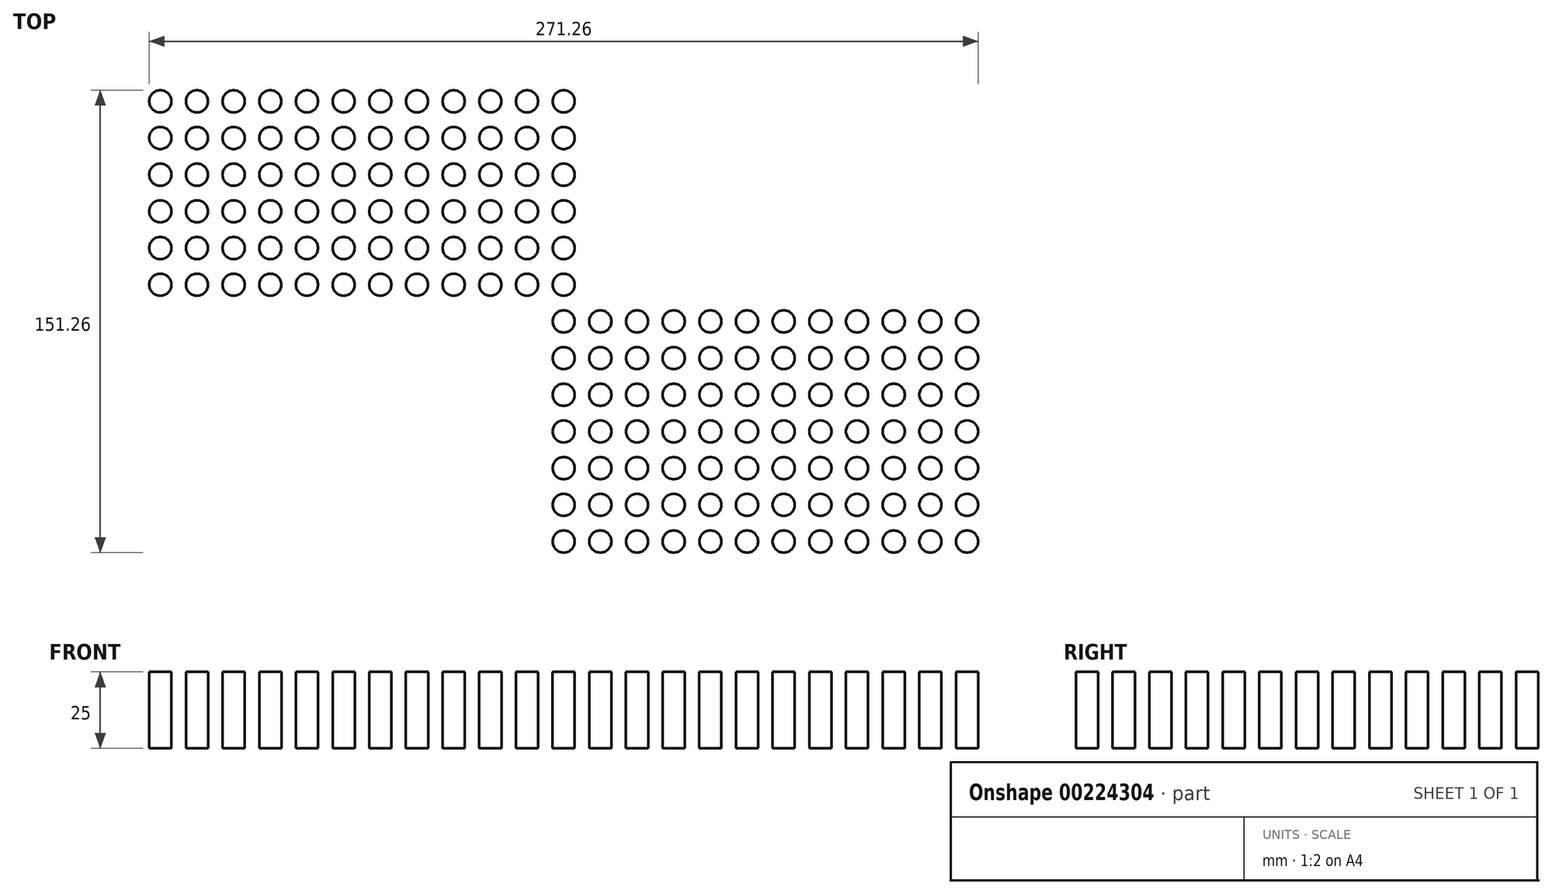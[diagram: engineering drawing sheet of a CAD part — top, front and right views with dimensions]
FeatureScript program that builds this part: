
annotation { "Feature Type Name" : "Feature", "Feature Type Description" : "" }
export const myFeature = defineFeature(function(context is Context, id is Id, definition is map)
    precondition{}
    {
        {
            var Q0;
            Q0=qCreatedBy(makeId("Top.planeOp"),FACE);
            var sketch = newSketch(context, id + "F0", { "sketchPlane" : qUnion([Q0])});
            skLineSegment(sketch, "E0.bottom", {"start": v(140, 90) * mm, "end": v(-140, 90) * mm});
            skLineSegment(sketch, "E0.top", {"start": v(140, -90) * mm, "end": v(-140, -90) * mm});
            skLineSegment(sketch, "E0.left", {"start": v(150, 80) * mm, "end": v(150, -80) * mm});
            skLineSegment(sketch, "E0.right", {"start": v(-150, 80) * mm, "end": v(-150, -80) * mm});
            skPoint(sketch, "E0.middle", {"position": v(0, 0) * mm});
            skPoint(sketch, "E1.visualSharp", {"position": v(-150, 90) * mm});
            skArc(sketch, "E1.filletArc", {"start": v(-140, 90) * mm, "mid": v(-147.07, 87.07) * mm, "end": v(-150, 80) * mm});
            skPoint(sketch, "E2.visualSharp", {"position": v(150, 90) * mm});
            skArc(sketch, "E2.filletArc", {"start": v(150, 80) * mm, "mid": v(147.07, 87.07) * mm, "end": v(140, 90) * mm});
            skPoint(sketch, "E3.visualSharp", {"position": v(150, -90) * mm});
            skArc(sketch, "E3.filletArc", {"start": v(140, -90) * mm, "mid": v(147.07, -87.07) * mm, "end": v(150, -80) * mm});
            skPoint(sketch, "E4.visualSharp", {"position": v(-150, -90) * mm});
            skArc(sketch, "E4.filletArc", {"start": v(-150, -80) * mm, "mid": v(-147.07, -87.07) * mm, "end": v(-140, -90) * mm});
            skSolve(sketch);
        }
        {
            var Q0;
            Q0=makeQuery(id+"F0.imprint","IMPRINT",FACE,{"disambiguationData":[TD([[makeQuery(id+"F0.imprint","IMPRINT",EDGE,{"derivedFrom":sQuery(id+"F0.wireOp",EDGE,"E0.bottom")}),1.0]])]});
            extrude(context, id + "F1", {"entities" : qUnion([Q0]), "depth" : 25 * mm});
        }
        {
            var Q0;
            Q0=makeQuery(id+"F1.opExtrude","CAP_FACE",FACE,{"disambiguationData":[OSD([sQuery(id+"F0.wireOp",EDGE,"E0.bottom"),sQuery(id+"F0.wireOp",EDGE,"E0.top"),sQuery(id+"F0.wireOp",EDGE,"E0.left"),sQuery(id+"F0.wireOp",EDGE,"E0.right"),sQuery(id+"F0.wireOp",EDGE,"E1.filletArc"),sQuery(id+"F0.wireOp",EDGE,"E2.filletArc"),sQuery(id+"F0.wireOp",EDGE,"E3.filletArc"),sQuery(id+"F0.wireOp",EDGE,"E4.filletArc")])],"isStart":false});
            var sketch = newSketch(context, id + "F2", { "sketchPlane" : qUnion([Q0])});
            skCircle(sketch, "E5", {"center": v(0, 0) * mm, "radius": 3.63 * mm});
            skCircle(sketch, "E6.0.1.0", {"center": v(0, 12) * mm, "radius": 3.63 * mm});
            skCircle(sketch, "E6.0.2.0", {"center": v(0, 24) * mm, "radius": 3.63 * mm});
            skCircle(sketch, "E6.0.3.0", {"center": v(0, 36) * mm, "radius": 3.63 * mm});
            skCircle(sketch, "E6.0.4.0", {"center": v(0, 48) * mm, "radius": 3.63 * mm});
            skCircle(sketch, "E6.0.5.0", {"center": v(0, 60) * mm, "radius": 3.63 * mm});
            skCircle(sketch, "E6.0.6.0", {"center": v(0, 72) * mm, "radius": 3.63 * mm});
            skCircle(sketch, "E6.1.0.0", {"center": v(12, 0) * mm, "radius": 3.63 * mm});
            skCircle(sketch, "E6.1.1.0", {"center": v(12, 12) * mm, "radius": 3.63 * mm});
            skCircle(sketch, "E6.1.2.0", {"center": v(12, 24) * mm, "radius": 3.63 * mm});
            skCircle(sketch, "E6.1.3.0", {"center": v(12, 36) * mm, "radius": 3.63 * mm});
            skCircle(sketch, "E6.1.4.0", {"center": v(12, 48) * mm, "radius": 3.63 * mm});
            skCircle(sketch, "E6.1.5.0", {"center": v(12, 60) * mm, "radius": 3.63 * mm});
            skCircle(sketch, "E6.1.6.0", {"center": v(12, 72) * mm, "radius": 3.63 * mm});
            skCircle(sketch, "E6.2.0.0", {"center": v(24, 0) * mm, "radius": 3.63 * mm});
            skCircle(sketch, "E6.2.1.0", {"center": v(24, 12) * mm, "radius": 3.63 * mm});
            skCircle(sketch, "E6.2.2.0", {"center": v(24, 24) * mm, "radius": 3.63 * mm});
            skCircle(sketch, "E6.2.3.0", {"center": v(24, 36) * mm, "radius": 3.63 * mm});
            skCircle(sketch, "E6.2.4.0", {"center": v(24, 48) * mm, "radius": 3.63 * mm});
            skCircle(sketch, "E6.2.5.0", {"center": v(24, 60) * mm, "radius": 3.63 * mm});
            skCircle(sketch, "E6.2.6.0", {"center": v(24, 72) * mm, "radius": 3.63 * mm});
            skCircle(sketch, "E6.3.0.0", {"center": v(36, 0) * mm, "radius": 3.63 * mm});
            skCircle(sketch, "E6.3.1.0", {"center": v(36, 12) * mm, "radius": 3.63 * mm});
            skCircle(sketch, "E6.3.2.0", {"center": v(36, 24) * mm, "radius": 3.63 * mm});
            skCircle(sketch, "E6.3.3.0", {"center": v(36, 36) * mm, "radius": 3.63 * mm});
            skCircle(sketch, "E6.3.4.0", {"center": v(36, 48) * mm, "radius": 3.63 * mm});
            skCircle(sketch, "E6.3.5.0", {"center": v(36, 60) * mm, "radius": 3.63 * mm});
            skCircle(sketch, "E6.3.6.0", {"center": v(36, 72) * mm, "radius": 3.63 * mm});
            skCircle(sketch, "E6.4.0.0", {"center": v(48, 0) * mm, "radius": 3.63 * mm});
            skCircle(sketch, "E6.4.1.0", {"center": v(48, 12) * mm, "radius": 3.63 * mm});
            skCircle(sketch, "E6.4.2.0", {"center": v(48, 24) * mm, "radius": 3.63 * mm});
            skCircle(sketch, "E6.4.3.0", {"center": v(48, 36) * mm, "radius": 3.63 * mm});
            skCircle(sketch, "E6.4.4.0", {"center": v(48, 48) * mm, "radius": 3.63 * mm});
            skCircle(sketch, "E6.4.5.0", {"center": v(48, 60) * mm, "radius": 3.63 * mm});
            skCircle(sketch, "E6.4.6.0", {"center": v(48, 72) * mm, "radius": 3.63 * mm});
            skCircle(sketch, "E6.5.0.0", {"center": v(60, 0) * mm, "radius": 3.63 * mm});
            skCircle(sketch, "E6.5.1.0", {"center": v(60, 12) * mm, "radius": 3.63 * mm});
            skCircle(sketch, "E6.5.2.0", {"center": v(60, 24) * mm, "radius": 3.63 * mm});
            skCircle(sketch, "E6.5.3.0", {"center": v(60, 36) * mm, "radius": 3.63 * mm});
            skCircle(sketch, "E6.5.4.0", {"center": v(60, 48) * mm, "radius": 3.63 * mm});
            skCircle(sketch, "E6.5.5.0", {"center": v(60, 60) * mm, "radius": 3.63 * mm});
            skCircle(sketch, "E6.5.6.0", {"center": v(60, 72) * mm, "radius": 3.63 * mm});
            skCircle(sketch, "E6.6.0.0", {"center": v(72, 0) * mm, "radius": 3.63 * mm});
            skCircle(sketch, "E6.6.1.0", {"center": v(72, 12) * mm, "radius": 3.63 * mm});
            skCircle(sketch, "E6.6.2.0", {"center": v(72, 24) * mm, "radius": 3.63 * mm});
            skCircle(sketch, "E6.6.3.0", {"center": v(72, 36) * mm, "radius": 3.63 * mm});
            skCircle(sketch, "E6.6.4.0", {"center": v(72, 48) * mm, "radius": 3.63 * mm});
            skCircle(sketch, "E6.6.5.0", {"center": v(72, 60) * mm, "radius": 3.63 * mm});
            skCircle(sketch, "E6.6.6.0", {"center": v(72, 72) * mm, "radius": 3.63 * mm});
            skCircle(sketch, "E6.7.0.0", {"center": v(84, 0) * mm, "radius": 3.63 * mm});
            skCircle(sketch, "E6.7.1.0", {"center": v(84, 12) * mm, "radius": 3.63 * mm});
            skCircle(sketch, "E6.7.2.0", {"center": v(84, 24) * mm, "radius": 3.63 * mm});
            skCircle(sketch, "E6.7.3.0", {"center": v(84, 36) * mm, "radius": 3.63 * mm});
            skCircle(sketch, "E6.7.4.0", {"center": v(84, 48) * mm, "radius": 3.63 * mm});
            skCircle(sketch, "E6.7.5.0", {"center": v(84, 60) * mm, "radius": 3.63 * mm});
            skCircle(sketch, "E6.7.6.0", {"center": v(84, 72) * mm, "radius": 3.63 * mm});
            skCircle(sketch, "E6.8.0.0", {"center": v(96, 0) * mm, "radius": 3.63 * mm});
            skCircle(sketch, "E6.8.1.0", {"center": v(96, 12) * mm, "radius": 3.63 * mm});
            skCircle(sketch, "E6.8.2.0", {"center": v(96, 24) * mm, "radius": 3.63 * mm});
            skCircle(sketch, "E6.8.3.0", {"center": v(96, 36) * mm, "radius": 3.63 * mm});
            skCircle(sketch, "E6.8.4.0", {"center": v(96, 48) * mm, "radius": 3.63 * mm});
            skCircle(sketch, "E6.8.5.0", {"center": v(96, 60) * mm, "radius": 3.63 * mm});
            skCircle(sketch, "E6.8.6.0", {"center": v(96, 72) * mm, "radius": 3.63 * mm});
            skCircle(sketch, "E6.9.0.0", {"center": v(108, 0) * mm, "radius": 3.63 * mm});
            skCircle(sketch, "E6.9.1.0", {"center": v(108, 12) * mm, "radius": 3.63 * mm});
            skCircle(sketch, "E6.9.2.0", {"center": v(108, 24) * mm, "radius": 3.63 * mm});
            skCircle(sketch, "E6.9.3.0", {"center": v(108, 36) * mm, "radius": 3.63 * mm});
            skCircle(sketch, "E6.9.4.0", {"center": v(108, 48) * mm, "radius": 3.63 * mm});
            skCircle(sketch, "E6.9.5.0", {"center": v(108, 60) * mm, "radius": 3.63 * mm});
            skCircle(sketch, "E6.9.6.0", {"center": v(108, 72) * mm, "radius": 3.63 * mm});
            skCircle(sketch, "E6.10.0.0", {"center": v(120, 0) * mm, "radius": 3.63 * mm});
            skCircle(sketch, "E6.10.1.0", {"center": v(120, 12) * mm, "radius": 3.63 * mm});
            skCircle(sketch, "E6.10.2.0", {"center": v(120, 24) * mm, "radius": 3.63 * mm});
            skCircle(sketch, "E6.10.3.0", {"center": v(120, 36) * mm, "radius": 3.63 * mm});
            skCircle(sketch, "E6.10.4.0", {"center": v(120, 48) * mm, "radius": 3.63 * mm});
            skCircle(sketch, "E6.10.5.0", {"center": v(120, 60) * mm, "radius": 3.63 * mm});
            skCircle(sketch, "E6.10.6.0", {"center": v(120, 72) * mm, "radius": 3.63 * mm});
            skCircle(sketch, "E6.11.0.0", {"center": v(132, 0) * mm, "radius": 3.63 * mm});
            skCircle(sketch, "E6.11.1.0", {"center": v(132, 12) * mm, "radius": 3.63 * mm});
            skCircle(sketch, "E6.11.2.0", {"center": v(132, 24) * mm, "radius": 3.63 * mm});
            skCircle(sketch, "E6.11.3.0", {"center": v(132, 36) * mm, "radius": 3.63 * mm});
            skCircle(sketch, "E6.11.4.0", {"center": v(132, 48) * mm, "radius": 3.63 * mm});
            skCircle(sketch, "E6.11.5.0", {"center": v(132, 60) * mm, "radius": 3.63 * mm});
            skCircle(sketch, "E6.11.6.0", {"center": v(132, 72) * mm, "radius": 3.63 * mm});
            skLineSegment(sketch, "E6.direction1", {"start": v(0, 0) * mm, "end": v(12, 0) * mm, "construction": true});
            skLineSegment(sketch, "E6.direction2", {"start": v(0, 0) * mm, "end": v(0, 12) * mm, "construction": true});
            skCircle(sketch, "E7.MirrorC", {"center": v(-84, 24) * mm, "radius": 3.63 * mm});
            skCircle(sketch, "E8.MirrorC", {"center": v(-108, 48) * mm, "radius": 3.63 * mm});
            skCircle(sketch, "E9.MirrorC", {"center": v(-132, 72) * mm, "radius": 3.63 * mm});
            skCircle(sketch, "E10.MirrorC", {"center": v(-24, 60) * mm, "radius": 3.63 * mm});
            skCircle(sketch, "E11.MirrorC", {"center": v(-60, 0) * mm, "radius": 3.63 * mm});
            skCircle(sketch, "E12.MirrorC", {"center": v(-36, 60) * mm, "radius": 3.63 * mm});
            skCircle(sketch, "E13.MirrorC", {"center": v(-72, 0) * mm, "radius": 3.63 * mm});
            skCircle(sketch, "E14.MirrorC", {"center": v(-96, 24) * mm, "radius": 3.63 * mm});
            skCircle(sketch, "E15.MirrorC", {"center": v(-120, 48) * mm, "radius": 3.63 * mm});
            skCircle(sketch, "E16.MirrorC", {"center": v(-84, 12) * mm, "radius": 3.63 * mm});
            skCircle(sketch, "E17.MirrorC", {"center": v(-108, 36) * mm, "radius": 3.63 * mm});
            skCircle(sketch, "E18.MirrorC", {"center": v(-132, 60) * mm, "radius": 3.63 * mm});
            skCircle(sketch, "E19.MirrorC", {"center": v(-24, 48) * mm, "radius": 3.63 * mm});
            skCircle(sketch, "E20.MirrorC", {"center": v(-48, 72) * mm, "radius": 3.63 * mm});
            skCircle(sketch, "E21.MirrorC", {"center": v(-12, 60) * mm, "radius": 3.63 * mm});
            skCircle(sketch, "E22.MirrorC", {"center": v(-36, 48) * mm, "radius": 3.63 * mm});
            skCircle(sketch, "E23.MirrorC", {"center": v(-60, 72) * mm, "radius": 3.63 * mm});
            skCircle(sketch, "E24.MirrorC", {"center": v(-96, 12) * mm, "radius": 3.63 * mm});
            skCircle(sketch, "E25.MirrorC", {"center": v(-120, 36) * mm, "radius": 3.63 * mm});
            skCircle(sketch, "E26.MirrorC", {"center": v(-12, 48) * mm, "radius": 3.63 * mm});
            skCircle(sketch, "E27.MirrorC", {"center": v(-12, 36) * mm, "radius": 3.63 * mm});
            skCircle(sketch, "E28.MirrorC", {"center": v(-12, 24) * mm, "radius": 3.63 * mm});
            skCircle(sketch, "E29.MirrorC", {"center": v(-12, 12) * mm, "radius": 3.63 * mm});
            skCircle(sketch, "E30.MirrorC", {"center": v(-12, 0) * mm, "radius": 3.63 * mm});
            skCircle(sketch, "E31.MirrorC", {"center": v(-24, 12) * mm, "radius": 3.63 * mm});
            skCircle(sketch, "E32.MirrorC", {"center": v(-24, 0) * mm, "radius": 3.63 * mm});
            skCircle(sketch, "E33.MirrorC", {"center": v(-12, 72) * mm, "radius": 3.63 * mm});
            skCircle(sketch, "E34.MirrorC", {"center": v(-84, 0) * mm, "radius": 3.63 * mm});
            skCircle(sketch, "E35.MirrorC", {"center": v(-108, 24) * mm, "radius": 3.63 * mm});
            skCircle(sketch, "E36.MirrorC", {"center": v(-132, 48) * mm, "radius": 3.63 * mm});
            skCircle(sketch, "E37.MirrorC", {"center": v(-24, 36) * mm, "radius": 3.63 * mm});
            skCircle(sketch, "E38.MirrorC", {"center": v(-48, 60) * mm, "radius": 3.63 * mm});
            skCircle(sketch, "E39.MirrorC", {"center": v(-36, 36) * mm, "radius": 3.63 * mm});
            skCircle(sketch, "E40.MirrorC", {"center": v(-60, 60) * mm, "radius": 3.63 * mm});
            skCircle(sketch, "E41.MirrorC", {"center": v(-96, 0) * mm, "radius": 3.63 * mm});
            skCircle(sketch, "E42.MirrorC", {"center": v(-120, 24) * mm, "radius": 3.63 * mm});
            skCircle(sketch, "E43.MirrorC", {"center": v(-24, 24) * mm, "radius": 3.63 * mm});
            skCircle(sketch, "E44.MirrorC", {"center": v(-48, 48) * mm, "radius": 3.63 * mm});
            skCircle(sketch, "E45.MirrorC", {"center": v(-36, 24) * mm, "radius": 3.63 * mm});
            skCircle(sketch, "E46.MirrorC", {"center": v(-60, 48) * mm, "radius": 3.63 * mm});
            skCircle(sketch, "E47.MirrorC", {"center": v(-84, 72) * mm, "radius": 3.63 * mm});
            skCircle(sketch, "E48.MirrorC", {"center": v(-120, 12) * mm, "radius": 3.63 * mm});
            skCircle(sketch, "E49.MirrorC", {"center": v(-72, 72) * mm, "radius": 3.63 * mm});
            skCircle(sketch, "E50.MirrorC", {"center": v(-108, 12) * mm, "radius": 3.63 * mm});
            skCircle(sketch, "E51.MirrorC", {"center": v(-132, 36) * mm, "radius": 3.63 * mm});
            skCircle(sketch, "E52.MirrorC", {"center": v(-72, 60) * mm, "radius": 3.63 * mm});
            skCircle(sketch, "E53.MirrorC", {"center": v(-84, 60) * mm, "radius": 3.63 * mm});
            skCircle(sketch, "E54.MirrorC", {"center": v(-120, 0) * mm, "radius": 3.63 * mm});
            skCircle(sketch, "E55.MirrorC", {"center": v(-108, 0) * mm, "radius": 3.63 * mm});
            skCircle(sketch, "E56.MirrorC", {"center": v(-132, 24) * mm, "radius": 3.63 * mm});
            skCircle(sketch, "E57.MirrorC", {"center": v(-36, 12) * mm, "radius": 3.63 * mm});
            skCircle(sketch, "E58.MirrorC", {"center": v(-60, 36) * mm, "radius": 3.63 * mm});
            skCircle(sketch, "E59.MirrorC", {"center": v(-48, 36) * mm, "radius": 3.63 * mm});
            skCircle(sketch, "E60.MirrorC", {"center": v(-84, 48) * mm, "radius": 3.63 * mm});
            skCircle(sketch, "E61.MirrorC", {"center": v(-72, 48) * mm, "radius": 3.63 * mm});
            skCircle(sketch, "E62.MirrorC", {"center": v(-96, 72) * mm, "radius": 3.63 * mm});
            skCircle(sketch, "E63.MirrorC", {"center": v(-108, 72) * mm, "radius": 3.63 * mm});
            skCircle(sketch, "E64.MirrorC", {"center": v(-132, 12) * mm, "radius": 3.63 * mm});
            skLineSegment(sketch, "E65.MirrorCS", {"start": v(0, 0) * mm, "end": v(-12, 0) * mm, "construction": true});
            skCircle(sketch, "E66.MirrorC", {"center": v(-36, 0) * mm, "radius": 3.63 * mm});
            skCircle(sketch, "E67.MirrorC", {"center": v(-60, 24) * mm, "radius": 3.63 * mm});
            skCircle(sketch, "E68.MirrorC", {"center": v(-48, 24) * mm, "radius": 3.63 * mm});
            skCircle(sketch, "E69.MirrorC", {"center": v(-48, 0) * mm, "radius": 3.63 * mm});
            skCircle(sketch, "E70.MirrorC", {"center": v(-72, 24) * mm, "radius": 3.63 * mm});
            skCircle(sketch, "E71.MirrorC", {"center": v(-96, 48) * mm, "radius": 3.63 * mm});
            skCircle(sketch, "E72.MirrorC", {"center": v(-120, 72) * mm, "radius": 3.63 * mm});
            skCircle(sketch, "E73.MirrorC", {"center": v(-72, 36) * mm, "radius": 3.63 * mm});
            skCircle(sketch, "E74.MirrorC", {"center": v(-84, 36) * mm, "radius": 3.63 * mm});
            skCircle(sketch, "E75.MirrorC", {"center": v(-96, 60) * mm, "radius": 3.63 * mm});
            skCircle(sketch, "E76.MirrorC", {"center": v(-108, 60) * mm, "radius": 3.63 * mm});
            skCircle(sketch, "E77.MirrorC", {"center": v(-132, 0) * mm, "radius": 3.63 * mm});
            skCircle(sketch, "E78.MirrorC", {"center": v(-24, 72) * mm, "radius": 3.63 * mm});
            skCircle(sketch, "E79.MirrorC", {"center": v(-60, 12) * mm, "radius": 3.63 * mm});
            skCircle(sketch, "E80.MirrorC", {"center": v(-48, 12) * mm, "radius": 3.63 * mm});
            skCircle(sketch, "E81.MirrorC", {"center": v(-120, 60) * mm, "radius": 3.63 * mm});
            skCircle(sketch, "E82.MirrorC", {"center": v(-72, 12) * mm, "radius": 3.63 * mm});
            skCircle(sketch, "E83.MirrorC", {"center": v(-96, 36) * mm, "radius": 3.63 * mm});
            skCircle(sketch, "E84.MirrorC", {"center": v(-36, 72) * mm, "radius": 3.63 * mm});
            skLineSegment(sketch, "E85.MirrorCS", {"start": v(0, 0) * mm, "end": v(0, -12) * mm, "construction": true});
            skCircle(sketch, "E86.MirrorC", {"center": v(0, -72) * mm, "radius": 3.63 * mm});
            skCircle(sketch, "E87.MirrorC", {"center": v(0, -24) * mm, "radius": 3.63 * mm});
            skCircle(sketch, "E88.MirrorC", {"center": v(0, -60) * mm, "radius": 3.63 * mm});
            skCircle(sketch, "E89.MirrorC", {"center": v(0, -48) * mm, "radius": 3.63 * mm});
            skCircle(sketch, "E90.MirrorC", {"center": v(0, -12) * mm, "radius": 3.63 * mm});
            skCircle(sketch, "E91.MirrorC", {"center": v(0, -36) * mm, "radius": 3.63 * mm});
            skCircle(sketch, "E92.MirrorC", {"center": v(-60, -24) * mm, "radius": 3.63 * mm});
            skCircle(sketch, "E93.MirrorC", {"center": v(-96, -36) * mm, "radius": 3.63 * mm});
            skCircle(sketch, "E94.MirrorC", {"center": v(-12, -36) * mm, "radius": 3.63 * mm});
            skCircle(sketch, "E95.MirrorC", {"center": v(-132, -48) * mm, "radius": 3.63 * mm});
            skCircle(sketch, "E96.MirrorC", {"center": v(-72, -60) * mm, "radius": 3.63 * mm});
            skCircle(sketch, "E97.MirrorC", {"center": v(36, -60) * mm, "radius": 3.63 * mm});
            skCircle(sketch, "E98.MirrorC", {"center": v(96, -24) * mm, "radius": 3.63 * mm});
            skCircle(sketch, "E99.MirrorC", {"center": v(120, -48) * mm, "radius": 3.63 * mm});
            skCircle(sketch, "E100.MirrorC", {"center": v(-72, -12) * mm, "radius": 3.63 * mm});
            skCircle(sketch, "E101.MirrorC", {"center": v(-24, -60) * mm, "radius": 3.63 * mm});
            skCircle(sketch, "E102.MirrorC", {"center": v(-12, -48) * mm, "radius": 3.63 * mm});
            skCircle(sketch, "E103.MirrorC", {"center": v(-108, -24) * mm, "radius": 3.63 * mm});
            skCircle(sketch, "E104.MirrorC", {"center": v(-132, -36) * mm, "radius": 3.63 * mm});
            skCircle(sketch, "E105.MirrorC", {"center": v(12, -60) * mm, "radius": 3.63 * mm});
            skCircle(sketch, "E106.MirrorC", {"center": v(36, -48) * mm, "radius": 3.63 * mm});
            skCircle(sketch, "E107.MirrorC", {"center": v(60, -72) * mm, "radius": 3.63 * mm});
            skCircle(sketch, "E108.MirrorC", {"center": v(96, -12) * mm, "radius": 3.63 * mm});
            skCircle(sketch, "E109.MirrorC", {"center": v(120, -36) * mm, "radius": 3.63 * mm});
            skCircle(sketch, "E110.MirrorC", {"center": v(12, -48) * mm, "radius": 3.63 * mm});
            skCircle(sketch, "E111.MirrorC", {"center": v(12, -36) * mm, "radius": 3.63 * mm});
            skCircle(sketch, "E112.MirrorC", {"center": v(12, -24) * mm, "radius": 3.63 * mm});
            skCircle(sketch, "E113.MirrorC", {"center": v(12, -12) * mm, "radius": 3.63 * mm});
            skCircle(sketch, "E114.MirrorC", {"center": v(-120, -60) * mm, "radius": 3.63 * mm});
            skCircle(sketch, "E115.MirrorC", {"center": v(24, -12) * mm, "radius": 3.63 * mm});
            skCircle(sketch, "E116.MirrorC", {"center": v(12, -72) * mm, "radius": 3.63 * mm});
            skCircle(sketch, "E117.MirrorC", {"center": v(-132, -72) * mm, "radius": 3.63 * mm});
            skCircle(sketch, "E118.MirrorC", {"center": v(-120, -36) * mm, "radius": 3.63 * mm});
            skCircle(sketch, "E119.MirrorC", {"center": v(-108, -12) * mm, "radius": 3.63 * mm});
            skCircle(sketch, "E120.MirrorC", {"center": v(36, -36) * mm, "radius": 3.63 * mm});
            skCircle(sketch, "E121.MirrorC", {"center": v(60, -60) * mm, "radius": 3.63 * mm});
            skCircle(sketch, "E122.MirrorC", {"center": v(120, -24) * mm, "radius": 3.63 * mm});
            skCircle(sketch, "E123.MirrorC", {"center": v(-48, -12) * mm, "radius": 3.63 * mm});
            skCircle(sketch, "E124.MirrorC", {"center": v(-108, -48) * mm, "radius": 3.63 * mm});
            skCircle(sketch, "E125.MirrorC", {"center": v(-96, -12) * mm, "radius": 3.63 * mm});
            skCircle(sketch, "E126.MirrorC", {"center": v(-12, -72) * mm, "radius": 3.63 * mm});
            skCircle(sketch, "E127.MirrorC", {"center": v(-72, -72) * mm, "radius": 3.63 * mm});
            skCircle(sketch, "E128.MirrorC", {"center": v(36, -24) * mm, "radius": 3.63 * mm});
            skCircle(sketch, "E129.MirrorC", {"center": v(60, -48) * mm, "radius": 3.63 * mm});
            skCircle(sketch, "E130.MirrorC", {"center": v(84, -72) * mm, "radius": 3.63 * mm});
            skCircle(sketch, "E131.MirrorC", {"center": v(120, -12) * mm, "radius": 3.63 * mm});
            skCircle(sketch, "E132.MirrorC", {"center": v(-120, -12) * mm, "radius": 3.63 * mm});
            skCircle(sketch, "E133.MirrorC", {"center": v(-132, -12) * mm, "radius": 3.63 * mm});
            skCircle(sketch, "E134.MirrorC", {"center": v(-60, -12) * mm, "radius": 3.63 * mm});
            skCircle(sketch, "E135.MirrorC", {"center": v(84, -60) * mm, "radius": 3.63 * mm});
            skCircle(sketch, "E136.MirrorC", {"center": v(-84, -24) * mm, "radius": 3.63 * mm});
            skCircle(sketch, "E137.MirrorC", {"center": v(-60, -72) * mm, "radius": 3.63 * mm});
            skCircle(sketch, "E138.MirrorC", {"center": v(36, -12) * mm, "radius": 3.63 * mm});
            skCircle(sketch, "E139.MirrorC", {"center": v(60, -36) * mm, "radius": 3.63 * mm});
            skCircle(sketch, "E140.MirrorC", {"center": v(-24, -12) * mm, "radius": 3.63 * mm});
            skCircle(sketch, "E141.MirrorC", {"center": v(-84, -72) * mm, "radius": 3.63 * mm});
            skCircle(sketch, "E142.MirrorC", {"center": v(-108, -72) * mm, "radius": 3.63 * mm});
            skCircle(sketch, "E143.MirrorC", {"center": v(-24, -72) * mm, "radius": 3.63 * mm});
            skCircle(sketch, "E144.MirrorC", {"center": v(84, -48) * mm, "radius": 3.63 * mm});
            skCircle(sketch, "E145.MirrorC", {"center": v(108, -72) * mm, "radius": 3.63 * mm});
            skCircle(sketch, "E146.MirrorC", {"center": v(-36, -48) * mm, "radius": 3.63 * mm});
            skCircle(sketch, "E147.MirrorC", {"center": v(60, -24) * mm, "radius": 3.63 * mm});
            skCircle(sketch, "E148.MirrorC", {"center": v(-60, -48) * mm, "radius": 3.63 * mm});
            skCircle(sketch, "E149.MirrorC", {"center": v(-96, -72) * mm, "radius": 3.63 * mm});
            skCircle(sketch, "E150.MirrorC", {"center": v(84, -36) * mm, "radius": 3.63 * mm});
            skCircle(sketch, "E151.MirrorC", {"center": v(108, -60) * mm, "radius": 3.63 * mm});
            skCircle(sketch, "E152.MirrorC", {"center": v(120, -60) * mm, "radius": 3.63 * mm});
            skCircle(sketch, "E153.MirrorC", {"center": v(96, -36) * mm, "radius": 3.63 * mm});
            skCircle(sketch, "E154.MirrorC", {"center": v(72, -12) * mm, "radius": 3.63 * mm});
            skCircle(sketch, "E155.MirrorC", {"center": v(36, -72) * mm, "radius": 3.63 * mm});
            skCircle(sketch, "E156.MirrorC", {"center": v(-84, -60) * mm, "radius": 3.63 * mm});
            skCircle(sketch, "E157.MirrorC", {"center": v(48, -60) * mm, "radius": 3.63 * mm});
            skCircle(sketch, "E158.MirrorC", {"center": v(-24, -36) * mm, "radius": 3.63 * mm});
            skCircle(sketch, "E159.MirrorC", {"center": v(-12, -24) * mm, "radius": 3.63 * mm});
            skCircle(sketch, "E160.MirrorC", {"center": v(24, -36) * mm, "radius": 3.63 * mm});
            skCircle(sketch, "E161.MirrorC", {"center": v(-36, -60) * mm, "radius": 3.63 * mm});
            skCircle(sketch, "E162.MirrorC", {"center": v(-36, -72) * mm, "radius": 3.63 * mm});
            skCircle(sketch, "E163.MirrorC", {"center": v(-48, -24) * mm, "radius": 3.63 * mm});
            skCircle(sketch, "E164.MirrorC", {"center": v(-132, -60) * mm, "radius": 3.63 * mm});
            skCircle(sketch, "E165.MirrorC", {"center": v(132, -48) * mm, "radius": 3.63 * mm});
            skCircle(sketch, "E166.MirrorC", {"center": v(48, -12) * mm, "radius": 3.63 * mm});
            skCircle(sketch, "E167.MirrorC", {"center": v(108, -24) * mm, "radius": 3.63 * mm});
            skCircle(sketch, "E168.MirrorC", {"center": v(-96, -24) * mm, "radius": 3.63 * mm});
            skCircle(sketch, "E169.MirrorC", {"center": v(96, -60) * mm, "radius": 3.63 * mm});
            skCircle(sketch, "E170.MirrorC", {"center": v(72, -36) * mm, "radius": 3.63 * mm});
            skCircle(sketch, "E171.MirrorC", {"center": v(-72, -24) * mm, "radius": 3.63 * mm});
            skCircle(sketch, "E172.MirrorC", {"center": v(24, -48) * mm, "radius": 3.63 * mm});
            skCircle(sketch, "E173.MirrorC", {"center": v(48, -72) * mm, "radius": 3.63 * mm});
            skCircle(sketch, "E174.MirrorC", {"center": v(-36, -36) * mm, "radius": 3.63 * mm});
            skCircle(sketch, "E175.MirrorC", {"center": v(120, -72) * mm, "radius": 3.63 * mm});
            skCircle(sketch, "E176.MirrorC", {"center": v(96, -48) * mm, "radius": 3.63 * mm});
            skCircle(sketch, "E177.MirrorC", {"center": v(72, -24) * mm, "radius": 3.63 * mm});
            skCircle(sketch, "E178.MirrorC", {"center": v(-48, -60) * mm, "radius": 3.63 * mm});
            skCircle(sketch, "E179.MirrorC", {"center": v(-12, -12) * mm, "radius": 3.63 * mm});
            skCircle(sketch, "E180.MirrorC", {"center": v(48, -24) * mm, "radius": 3.63 * mm});
            skCircle(sketch, "E181.MirrorC", {"center": v(-120, -48) * mm, "radius": 3.63 * mm});
            skCircle(sketch, "E182.MirrorC", {"center": v(132, -12) * mm, "radius": 3.63 * mm});
            skCircle(sketch, "E183.MirrorC", {"center": v(96, -72) * mm, "radius": 3.63 * mm});
            skCircle(sketch, "E184.MirrorC", {"center": v(72, -48) * mm, "radius": 3.63 * mm});
            skCircle(sketch, "E185.MirrorC", {"center": v(-96, -48) * mm, "radius": 3.63 * mm});
            skCircle(sketch, "E186.MirrorC", {"center": v(-24, -48) * mm, "radius": 3.63 * mm});
            skCircle(sketch, "E187.MirrorC", {"center": v(-132, -24) * mm, "radius": 3.63 * mm});
            skCircle(sketch, "E188.MirrorC", {"center": v(-60, -60) * mm, "radius": 3.63 * mm});
            skCircle(sketch, "E189.MirrorC", {"center": v(132, -60) * mm, "radius": 3.63 * mm});
            skCircle(sketch, "E190.MirrorC", {"center": v(108, -36) * mm, "radius": 3.63 * mm});
            skCircle(sketch, "E191.MirrorC", {"center": v(84, -12) * mm, "radius": 3.63 * mm});
            skCircle(sketch, "E192.MirrorC", {"center": v(-96, -60) * mm, "radius": 3.63 * mm});
            skCircle(sketch, "E193.MirrorC", {"center": v(48, -36) * mm, "radius": 3.63 * mm});
            skCircle(sketch, "E194.MirrorC", {"center": v(-84, -12) * mm, "radius": 3.63 * mm});
            skCircle(sketch, "E195.MirrorC", {"center": v(132, -24) * mm, "radius": 3.63 * mm});
            skCircle(sketch, "E196.MirrorC", {"center": v(-84, -48) * mm, "radius": 3.63 * mm});
            skCircle(sketch, "E197.MirrorC", {"center": v(72, -60) * mm, "radius": 3.63 * mm});
            skCircle(sketch, "E198.MirrorC", {"center": v(-48, -48) * mm, "radius": 3.63 * mm});
            skCircle(sketch, "E199.MirrorC", {"center": v(-120, -72) * mm, "radius": 3.63 * mm});
            skCircle(sketch, "E200.MirrorC", {"center": v(-36, -12) * mm, "radius": 3.63 * mm});
            skCircle(sketch, "E201.MirrorC", {"center": v(-108, -36) * mm, "radius": 3.63 * mm});
            skCircle(sketch, "E202.MirrorC", {"center": v(132, -36) * mm, "radius": 3.63 * mm});
            skCircle(sketch, "E203.MirrorC", {"center": v(24, -60) * mm, "radius": 3.63 * mm});
            skCircle(sketch, "E204.MirrorC", {"center": v(-48, -72) * mm, "radius": 3.63 * mm});
            skCircle(sketch, "E205.MirrorC", {"center": v(132, -72) * mm, "radius": 3.63 * mm});
            skCircle(sketch, "E206.MirrorC", {"center": v(108, -12) * mm, "radius": 3.63 * mm});
            skCircle(sketch, "E207.MirrorC", {"center": v(72, -72) * mm, "radius": 3.63 * mm});
            skCircle(sketch, "E208.MirrorC", {"center": v(108, -48) * mm, "radius": 3.63 * mm});
            skCircle(sketch, "E209.MirrorC", {"center": v(84, -24) * mm, "radius": 3.63 * mm});
            skCircle(sketch, "E210.MirrorC", {"center": v(-72, -36) * mm, "radius": 3.63 * mm});
            skCircle(sketch, "E211.MirrorC", {"center": v(-60, -36) * mm, "radius": 3.63 * mm});
            skCircle(sketch, "E212.MirrorC", {"center": v(-108, -60) * mm, "radius": 3.63 * mm});
            skCircle(sketch, "E213.MirrorC", {"center": v(-120, -24) * mm, "radius": 3.63 * mm});
            skCircle(sketch, "E214.MirrorC", {"center": v(-72, -48) * mm, "radius": 3.63 * mm});
            skCircle(sketch, "E215.MirrorC", {"center": v(-36, -24) * mm, "radius": 3.63 * mm});
            skCircle(sketch, "E216.MirrorC", {"center": v(48, -48) * mm, "radius": 3.63 * mm});
            skCircle(sketch, "E217.MirrorC", {"center": v(24, -24) * mm, "radius": 3.63 * mm});
            skCircle(sketch, "E218.MirrorC", {"center": v(60, -12) * mm, "radius": 3.63 * mm});
            skCircle(sketch, "E219.MirrorC", {"center": v(-84, -36) * mm, "radius": 3.63 * mm});
            skCircle(sketch, "E220.MirrorC", {"center": v(-48, -36) * mm, "radius": 3.63 * mm});
            skCircle(sketch, "E221.MirrorC", {"center": v(-24, -24) * mm, "radius": 3.63 * mm});
            skCircle(sketch, "E222.MirrorC", {"center": v(24, -72) * mm, "radius": 3.63 * mm});
            skCircle(sketch, "E223.MirrorC", {"center": v(-12, -60) * mm, "radius": 3.63 * mm});
            skSolve(sketch);
        }
        {
            var Q0;
            Q0=makeQuery(id+"F2.imprint","IMPRINT",FACE,{"disambiguationData":[TD([[makeQuery(id+"F2.imprint","IMPRINT",EDGE,{"derivedFrom":sQuery(id+"F2.wireOp",EDGE,"E6.2.1.0")}),1.0]])]});
            var Q1;
            Q1=makeQuery(id+"F2.imprint","IMPRINT",FACE,{"disambiguationData":[TD([[makeQuery(id+"F2.imprint","IMPRINT",EDGE,{"derivedFrom":sQuery(id+"F2.wireOp",EDGE,"E6.2.2.0")}),1.0]])]});
            var Q2;
            Q2=makeQuery(id+"F2.imprint","IMPRINT",FACE,{"disambiguationData":[TD([[makeQuery(id+"F2.imprint","IMPRINT",EDGE,{"derivedFrom":sQuery(id+"F2.wireOp",EDGE,"E6.2.3.0")}),1.0]])]});
            var Q3;
            Q3=makeQuery(id+"F2.imprint","IMPRINT",FACE,{"disambiguationData":[TD([[makeQuery(id+"F2.imprint","IMPRINT",EDGE,{"derivedFrom":sQuery(id+"F2.wireOp",EDGE,"E6.2.5.0")}),1.0]])]});
            var Q4;
            Q4=makeQuery(id+"F2.imprint","IMPRINT",FACE,{"disambiguationData":[TD([[makeQuery(id+"F2.imprint","IMPRINT",EDGE,{"derivedFrom":sQuery(id+"F2.wireOp",EDGE,"E6.3.1.0")}),1.0]])]});
            var Q5;
            Q5=makeQuery(id+"F2.imprint","IMPRINT",FACE,{"disambiguationData":[TD([[makeQuery(id+"F2.imprint","IMPRINT",EDGE,{"derivedFrom":sQuery(id+"F2.wireOp",EDGE,"E6.3.2.0")}),1.0]])]});
            var Q6;
            Q6=makeQuery(id+"F2.imprint","IMPRINT",FACE,{"disambiguationData":[TD([[makeQuery(id+"F2.imprint","IMPRINT",EDGE,{"derivedFrom":sQuery(id+"F2.wireOp",EDGE,"E6.1.3.0")}),1.0]])]});
            var Q7;
            Q7=makeQuery(id+"F2.imprint","IMPRINT",FACE,{"disambiguationData":[TD([[makeQuery(id+"F2.imprint","IMPRINT",EDGE,{"derivedFrom":sQuery(id+"F2.wireOp",EDGE,"E6.1.4.0")}),1.0]])]});
            var Q8;
            Q8=makeQuery(id+"F2.imprint","IMPRINT",FACE,{"disambiguationData":[TD([[makeQuery(id+"F2.imprint","IMPRINT",EDGE,{"derivedFrom":sQuery(id+"F2.wireOp",EDGE,"E6.2.4.0")}),1.0]])]});
            var Q9;
            Q9=makeQuery(id+"F2.imprint","IMPRINT",FACE,{"disambiguationData":[TD([[makeQuery(id+"F2.imprint","IMPRINT",EDGE,{"derivedFrom":sQuery(id+"F2.wireOp",EDGE,"E6.1.5.0")}),1.0]])]});
            var Q10;
            Q10=makeQuery(id+"F2.imprint","IMPRINT",FACE,{"disambiguationData":[TD([[makeQuery(id+"F2.imprint","IMPRINT",EDGE,{"derivedFrom":sQuery(id+"F2.wireOp",EDGE,"E6.1.1.0")}),1.0]])]});
            var Q11;
            Q11=makeQuery(id+"F2.imprint","IMPRINT",FACE,{"disambiguationData":[TD([[makeQuery(id+"F2.imprint","IMPRINT",EDGE,{"derivedFrom":sQuery(id+"F2.wireOp",EDGE,"E6.3.3.0")}),1.0]])]});
            var Q12;
            Q12=makeQuery(id+"F2.imprint","IMPRINT",FACE,{"disambiguationData":[TD([[makeQuery(id+"F2.imprint","IMPRINT",EDGE,{"derivedFrom":sQuery(id+"F2.wireOp",EDGE,"E6.1.2.0")}),1.0]])]});
            var Q13;
            Q13=makeQuery(id+"F2.imprint","IMPRINT",FACE,{"disambiguationData":[TD([[makeQuery(id+"F2.imprint","IMPRINT",EDGE,{"derivedFrom":sQuery(id+"F2.wireOp",EDGE,"E6.2.6.0")}),1.0]])]});
            var Q14;
            Q14=makeQuery(id+"F2.imprint","IMPRINT",FACE,{"disambiguationData":[TD([[makeQuery(id+"F2.imprint","IMPRINT",EDGE,{"derivedFrom":sQuery(id+"F2.wireOp",EDGE,"E6.1.6.0")}),1.0]])]});
            var Q15;
            Q15=makeQuery(id+"F2.imprint","IMPRINT",FACE,{"disambiguationData":[TD([[makeQuery(id+"F2.imprint","IMPRINT",EDGE,{"derivedFrom":sQuery(id+"F2.wireOp",EDGE,"E6.3.4.0")}),1.0]])]});
            var Q16;
            Q16=makeQuery(id+"F2.imprint","IMPRINT",FACE,{"disambiguationData":[TD([[makeQuery(id+"F2.imprint","IMPRINT",EDGE,{"derivedFrom":sQuery(id+"F2.wireOp",EDGE,"E209.MirrorC")}),-1.0]])]});
            var Q17;
            Q17=makeQuery(id+"F2.imprint","IMPRINT",FACE,{"disambiguationData":[TD([[makeQuery(id+"F2.imprint","IMPRINT",EDGE,{"derivedFrom":sQuery(id+"F2.wireOp",EDGE,"E156.MirrorC")}),1.0]])]});
            var Q18;
            Q18=makeQuery(id+"F2.imprint","IMPRINT",FACE,{"disambiguationData":[TD([[makeQuery(id+"F2.imprint","IMPRINT",EDGE,{"derivedFrom":sQuery(id+"F2.wireOp",EDGE,"E170.MirrorC")}),-1.0]])]});
            var Q19;
            Q19=makeQuery(id+"F2.imprint","IMPRINT",FACE,{"disambiguationData":[TD([[makeQuery(id+"F2.imprint","IMPRINT",EDGE,{"derivedFrom":sQuery(id+"F2.wireOp",EDGE,"E180.MirrorC")}),-1.0]])]});
            var Q20;
            Q20=makeQuery(id+"F2.imprint","IMPRINT",FACE,{"disambiguationData":[TD([[makeQuery(id+"F2.imprint","IMPRINT",EDGE,{"derivedFrom":sQuery(id+"F2.wireOp",EDGE,"E6.9.0.0")}),-1.0]])]});
            var Q21;
            Q21=makeQuery(id+"F2.imprint","IMPRINT",FACE,{"disambiguationData":[TD([[makeQuery(id+"F2.imprint","IMPRINT",EDGE,{"derivedFrom":sQuery(id+"F2.wireOp",EDGE,"E107.MirrorC")}),-1.0]])]});
            var Q22;
            Q22=makeQuery(id+"F2.imprint","IMPRINT",FACE,{"disambiguationData":[TD([[makeQuery(id+"F2.imprint","IMPRINT",EDGE,{"derivedFrom":sQuery(id+"F2.wireOp",EDGE,"E115.MirrorC")}),-1.0]])]});
            var Q23;
            Q23=makeQuery(id+"F2.imprint","IMPRINT",FACE,{"disambiguationData":[TD([[makeQuery(id+"F2.imprint","IMPRINT",EDGE,{"derivedFrom":sQuery(id+"F2.wireOp",EDGE,"E128.MirrorC")}),-1.0]])]});
            var Q24;
            Q24=makeQuery(id+"F2.imprint","IMPRINT",FACE,{"disambiguationData":[TD([[makeQuery(id+"F2.imprint","IMPRINT",EDGE,{"derivedFrom":sQuery(id+"F2.wireOp",EDGE,"E142.MirrorC")}),1.0]])]});
            var Q25;
            Q25=makeQuery(id+"F2.imprint","IMPRINT",FACE,{"disambiguationData":[TD([[makeQuery(id+"F2.imprint","IMPRINT",EDGE,{"derivedFrom":sQuery(id+"F2.wireOp",EDGE,"E6.0.1.0")}),-1.0]])]});
            var Q26;
            Q26=makeQuery(id+"F2.imprint","IMPRINT",FACE,{"disambiguationData":[TD([[makeQuery(id+"F2.imprint","IMPRINT",EDGE,{"derivedFrom":sQuery(id+"F2.wireOp",EDGE,"E49.MirrorC")}),-1.0]])]});
            var Q27;
            Q27=makeQuery(id+"F2.imprint","IMPRINT",FACE,{"disambiguationData":[TD([[makeQuery(id+"F2.imprint","IMPRINT",EDGE,{"derivedFrom":sQuery(id+"F2.wireOp",EDGE,"E70.MirrorC")}),-1.0]])]});
            var Q28;
            Q28=makeQuery(id+"F2.imprint","IMPRINT",FACE,{"disambiguationData":[TD([[makeQuery(id+"F2.imprint","IMPRINT",EDGE,{"derivedFrom":sQuery(id+"F2.wireOp",EDGE,"E11.MirrorC")}),1.0]])]});
            var Q29;
            Q29=makeQuery(id+"F2.imprint","IMPRINT",FACE,{"disambiguationData":[TD([[makeQuery(id+"F2.imprint","IMPRINT",EDGE,{"derivedFrom":sQuery(id+"F2.wireOp",EDGE,"E6.5.5.0")}),1.0]])]});
            var Q30;
            Q30=makeQuery(id+"F2.imprint","IMPRINT",FACE,{"disambiguationData":[TD([[makeQuery(id+"F2.imprint","IMPRINT",EDGE,{"derivedFrom":sQuery(id+"F2.wireOp",EDGE,"E6.8.3.0")}),1.0]])]});
            var Q31;
            Q31=makeQuery(id+"F2.imprint","IMPRINT",FACE,{"disambiguationData":[TD([[makeQuery(id+"F2.imprint","IMPRINT",EDGE,{"derivedFrom":sQuery(id+"F2.wireOp",EDGE,"E6.11.1.0")}),1.0]])]});
            var Q32;
            Q32=makeQuery(id+"F2.imprint","IMPRINT",FACE,{"disambiguationData":[TD([[makeQuery(id+"F2.imprint","IMPRINT",EDGE,{"derivedFrom":sQuery(id+"F2.wireOp",EDGE,"E19.MirrorC")}),-1.0]])]});
            var Q33;
            Q33=makeQuery(id+"F2.imprint","IMPRINT",FACE,{"disambiguationData":[TD([[makeQuery(id+"F2.imprint","IMPRINT",EDGE,{"derivedFrom":sQuery(id+"F2.wireOp",EDGE,"E208.MirrorC")}),-1.0]])]});
            var Q34;
            Q34=makeQuery(id+"F2.imprint","IMPRINT",FACE,{"disambiguationData":[TD([[makeQuery(id+"F2.imprint","IMPRINT",EDGE,{"derivedFrom":sQuery(id+"F2.wireOp",EDGE,"E155.MirrorC")}),-1.0]])]});
            var Q35;
            Q35=makeQuery(id+"F2.imprint","IMPRINT",FACE,{"disambiguationData":[TD([[makeQuery(id+"F2.imprint","IMPRINT",EDGE,{"derivedFrom":sQuery(id+"F2.wireOp",EDGE,"E169.MirrorC")}),-1.0]])]});
            var Q36;
            Q36=makeQuery(id+"F2.imprint","IMPRINT",FACE,{"disambiguationData":[TD([[makeQuery(id+"F2.imprint","IMPRINT",EDGE,{"derivedFrom":sQuery(id+"F2.wireOp",EDGE,"E69.MirrorC")}),1.0]])]});
            var Q37;
            Q37=makeQuery(id+"F2.imprint","IMPRINT",FACE,{"disambiguationData":[TD([[makeQuery(id+"F2.imprint","IMPRINT",EDGE,{"derivedFrom":sQuery(id+"F2.wireOp",EDGE,"E195.MirrorC")}),-1.0]])]});
            var Q38;
            Q38=makeQuery(id+"F2.imprint","IMPRINT",FACE,{"disambiguationData":[TD([[makeQuery(id+"F2.imprint","IMPRINT",EDGE,{"derivedFrom":sQuery(id+"F2.wireOp",EDGE,"E106.MirrorC")}),-1.0]])]});
            var Q39;
            Q39=makeQuery(id+"F2.imprint","IMPRINT",FACE,{"disambiguationData":[TD([[makeQuery(id+"F2.imprint","IMPRINT",EDGE,{"derivedFrom":sQuery(id+"F2.wireOp",EDGE,"E127.MirrorC")}),1.0]])]});
            var Q40;
            Q40=makeQuery(id+"F2.imprint","IMPRINT",FACE,{"disambiguationData":[TD([[makeQuery(id+"F2.imprint","IMPRINT",EDGE,{"derivedFrom":sQuery(id+"F2.wireOp",EDGE,"E141.MirrorC")}),1.0]])]});
            var Q41;
            Q41=makeQuery(id+"F2.imprint","IMPRINT",FACE,{"disambiguationData":[TD([[makeQuery(id+"F2.imprint","IMPRINT",EDGE,{"derivedFrom":sQuery(id+"F2.wireOp",EDGE,"E6.0.2.0")}),-1.0]])]});
            var Q42;
            Q42=makeQuery(id+"F2.imprint","IMPRINT",FACE,{"disambiguationData":[TD([[makeQuery(id+"F2.imprint","IMPRINT",EDGE,{"derivedFrom":sQuery(id+"F2.wireOp",EDGE,"E48.MirrorC")}),-1.0]])]});
            var Q43;
            Q43=makeQuery(id+"F2.imprint","IMPRINT",FACE,{"disambiguationData":[TD([[makeQuery(id+"F2.imprint","IMPRINT",EDGE,{"derivedFrom":sQuery(id+"F2.wireOp",EDGE,"E68.MirrorC")}),-1.0]])]});
            var Q44;
            Q44=makeQuery(id+"F2.imprint","IMPRINT",FACE,{"disambiguationData":[TD([[makeQuery(id+"F2.imprint","IMPRINT",EDGE,{"derivedFrom":sQuery(id+"F2.wireOp",EDGE,"E93.MirrorC")}),1.0]])]});
            var Q45;
            Q45=makeQuery(id+"F2.imprint","IMPRINT",FACE,{"disambiguationData":[TD([[makeQuery(id+"F2.imprint","IMPRINT",EDGE,{"derivedFrom":sQuery(id+"F2.wireOp",EDGE,"E6.5.4.0")}),1.0]])]});
            var Q46;
            Q46=makeQuery(id+"F2.imprint","IMPRINT",FACE,{"disambiguationData":[TD([[makeQuery(id+"F2.imprint","IMPRINT",EDGE,{"derivedFrom":sQuery(id+"F2.wireOp",EDGE,"E6.8.2.0")}),1.0]])]});
            var Q47;
            Q47=makeQuery(id+"F2.imprint","IMPRINT",FACE,{"disambiguationData":[TD([[makeQuery(id+"F2.imprint","IMPRINT",EDGE,{"derivedFrom":sQuery(id+"F2.wireOp",EDGE,"E6.10.6.0")}),1.0]])]});
            var Q48;
            Q48=makeQuery(id+"F2.imprint","IMPRINT",FACE,{"disambiguationData":[TD([[makeQuery(id+"F2.imprint","IMPRINT",EDGE,{"derivedFrom":sQuery(id+"F2.wireOp",EDGE,"E18.MirrorC")}),-1.0]])]});
            var Q49;
            Q49=makeQuery(id+"F2.imprint","IMPRINT",FACE,{"disambiguationData":[TD([[makeQuery(id+"F2.imprint","IMPRINT",EDGE,{"derivedFrom":sQuery(id+"F2.wireOp",EDGE,"E154.MirrorC")}),-1.0]])]});
            var Q50;
            Q50=makeQuery(id+"F2.imprint","IMPRINT",FACE,{"disambiguationData":[TD([[makeQuery(id+"F2.imprint","IMPRINT",EDGE,{"derivedFrom":sQuery(id+"F2.wireOp",EDGE,"E6.11.0.0")}),-1.0]])]});
            var Q51;
            Q51=makeQuery(id+"F2.imprint","IMPRINT",FACE,{"disambiguationData":[TD([[makeQuery(id+"F2.imprint","IMPRINT",EDGE,{"derivedFrom":sQuery(id+"F2.wireOp",EDGE,"E13.MirrorC")}),1.0]])]});
            var Q52;
            Q52=makeQuery(id+"F2.imprint","IMPRINT",FACE,{"disambiguationData":[TD([[makeQuery(id+"F2.imprint","IMPRINT",EDGE,{"derivedFrom":sQuery(id+"F2.wireOp",EDGE,"E194.MirrorC")}),1.0]])]});
            var Q53;
            Q53=makeQuery(id+"F2.imprint","IMPRINT",FACE,{"disambiguationData":[TD([[makeQuery(id+"F2.imprint","IMPRINT",EDGE,{"derivedFrom":sQuery(id+"F2.wireOp",EDGE,"E105.MirrorC")}),-1.0]])]});
            var Q54;
            Q54=makeQuery(id+"F2.imprint","IMPRINT",FACE,{"disambiguationData":[TD([[makeQuery(id+"F2.imprint","IMPRINT",EDGE,{"derivedFrom":sQuery(id+"F2.wireOp",EDGE,"E114.MirrorC")}),1.0]])]});
            var Q55;
            Q55=makeQuery(id+"F2.imprint","IMPRINT",FACE,{"disambiguationData":[TD([[makeQuery(id+"F2.imprint","IMPRINT",EDGE,{"derivedFrom":sQuery(id+"F2.wireOp",EDGE,"E126.MirrorC")}),1.0]])]});
            var Q56;
            Q56=makeQuery(id+"F2.imprint","IMPRINT",FACE,{"disambiguationData":[TD([[makeQuery(id+"F2.imprint","IMPRINT",EDGE,{"derivedFrom":sQuery(id+"F2.wireOp",EDGE,"E140.MirrorC")}),1.0]])]});
            var Q57;
            Q57=makeQuery(id+"F2.imprint","IMPRINT",FACE,{"disambiguationData":[TD([[makeQuery(id+"F2.imprint","IMPRINT",EDGE,{"derivedFrom":sQuery(id+"F2.wireOp",EDGE,"E6.0.3.0")}),-1.0]])]});
            var Q58;
            Q58=makeQuery(id+"F2.imprint","IMPRINT",FACE,{"disambiguationData":[TD([[makeQuery(id+"F2.imprint","IMPRINT",EDGE,{"derivedFrom":sQuery(id+"F2.wireOp",EDGE,"E47.MirrorC")}),-1.0]])]});
            var Q59;
            Q59=makeQuery(id+"F2.imprint","IMPRINT",FACE,{"disambiguationData":[TD([[makeQuery(id+"F2.imprint","IMPRINT",EDGE,{"derivedFrom":sQuery(id+"F2.wireOp",EDGE,"E67.MirrorC")}),-1.0]])]});
            var Q60;
            Q60=makeQuery(id+"F2.imprint","IMPRINT",FACE,{"disambiguationData":[TD([[makeQuery(id+"F2.imprint","IMPRINT",EDGE,{"derivedFrom":sQuery(id+"F2.wireOp",EDGE,"E92.MirrorC")}),1.0]])]});
            var Q61;
            Q61=makeQuery(id+"F2.imprint","IMPRINT",FACE,{"disambiguationData":[TD([[makeQuery(id+"F2.imprint","IMPRINT",EDGE,{"derivedFrom":sQuery(id+"F2.wireOp",EDGE,"E6.5.3.0")}),1.0]])]});
            var Q62;
            Q62=makeQuery(id+"F2.imprint","IMPRINT",FACE,{"disambiguationData":[TD([[makeQuery(id+"F2.imprint","IMPRINT",EDGE,{"derivedFrom":sQuery(id+"F2.wireOp",EDGE,"E6.8.1.0")}),1.0]])]});
            var Q63;
            Q63=makeQuery(id+"F2.imprint","IMPRINT",FACE,{"disambiguationData":[TD([[makeQuery(id+"F2.imprint","IMPRINT",EDGE,{"derivedFrom":sQuery(id+"F2.wireOp",EDGE,"E6.10.5.0")}),1.0]])]});
            var Q64;
            Q64=makeQuery(id+"F2.imprint","IMPRINT",FACE,{"disambiguationData":[TD([[makeQuery(id+"F2.imprint","IMPRINT",EDGE,{"derivedFrom":sQuery(id+"F2.wireOp",EDGE,"E17.MirrorC")}),-1.0]])]});
            var Q65;
            Q65=makeQuery(id+"F2.imprint","IMPRINT",FACE,{"disambiguationData":[TD([[makeQuery(id+"F2.imprint","IMPRINT",EDGE,{"derivedFrom":sQuery(id+"F2.wireOp",EDGE,"E207.MirrorC")}),-1.0]])]});
            var Q66;
            Q66=makeQuery(id+"F2.imprint","IMPRINT",FACE,{"disambiguationData":[TD([[makeQuery(id+"F2.imprint","IMPRINT",EDGE,{"derivedFrom":sQuery(id+"F2.wireOp",EDGE,"E223.MirrorC")}),1.0]])]});
            var Q67;
            Q67=makeQuery(id+"F2.imprint","IMPRINT",FACE,{"disambiguationData":[TD([[makeQuery(id+"F2.imprint","IMPRINT",EDGE,{"derivedFrom":sQuery(id+"F2.wireOp",EDGE,"E104.MirrorC")}),1.0]])]});
            var Q68;
            Q68=makeQuery(id+"F2.imprint","IMPRINT",FACE,{"disambiguationData":[TD([[makeQuery(id+"F2.imprint","IMPRINT",EDGE,{"derivedFrom":sQuery(id+"F2.wireOp",EDGE,"E90.MirrorC")}),-1.0]])]});
            var Q69;
            Q69=makeQuery(id+"F2.imprint","IMPRINT",FACE,{"disambiguationData":[TD([[makeQuery(id+"F2.imprint","IMPRINT",EDGE,{"derivedFrom":sQuery(id+"F2.wireOp",EDGE,"E125.MirrorC")}),1.0]])]});
            var Q70;
            Q70=makeQuery(id+"F2.imprint","IMPRINT",FACE,{"disambiguationData":[TD([[makeQuery(id+"F2.imprint","IMPRINT",EDGE,{"derivedFrom":sQuery(id+"F2.wireOp",EDGE,"E139.MirrorC")}),-1.0]])]});
            var Q71;
            Q71=makeQuery(id+"F2.imprint","IMPRINT",FACE,{"disambiguationData":[TD([[makeQuery(id+"F2.imprint","IMPRINT",EDGE,{"derivedFrom":sQuery(id+"F2.wireOp",EDGE,"E6.0.4.0")}),-1.0]])]});
            var Q72;
            Q72=makeQuery(id+"F2.imprint","IMPRINT",FACE,{"disambiguationData":[TD([[makeQuery(id+"F2.imprint","IMPRINT",EDGE,{"derivedFrom":sQuery(id+"F2.wireOp",EDGE,"E46.MirrorC")}),-1.0]])]});
            var Q73;
            Q73=makeQuery(id+"F2.imprint","IMPRINT",FACE,{"disambiguationData":[TD([[makeQuery(id+"F2.imprint","IMPRINT",EDGE,{"derivedFrom":sQuery(id+"F2.wireOp",EDGE,"E64.MirrorC")}),-1.0]])]});
            var Q74;
            Q74=makeQuery(id+"F2.imprint","IMPRINT",FACE,{"disambiguationData":[TD([[makeQuery(id+"F2.imprint","IMPRINT",EDGE,{"derivedFrom":sQuery(id+"F2.wireOp",EDGE,"E84.MirrorC")}),-1.0]])]});
            var Q75;
            Q75=makeQuery(id+"F2.imprint","IMPRINT",FACE,{"disambiguationData":[TD([[makeQuery(id+"F2.imprint","IMPRINT",EDGE,{"derivedFrom":sQuery(id+"F2.wireOp",EDGE,"E6.5.2.0")}),1.0]])]});
            var Q76;
            Q76=makeQuery(id+"F2.imprint","IMPRINT",FACE,{"disambiguationData":[TD([[makeQuery(id+"F2.imprint","IMPRINT",EDGE,{"derivedFrom":sQuery(id+"F2.wireOp",EDGE,"E6.7.6.0")}),1.0]])]});
            var Q77;
            Q77=makeQuery(id+"F2.imprint","IMPRINT",FACE,{"disambiguationData":[TD([[makeQuery(id+"F2.imprint","IMPRINT",EDGE,{"derivedFrom":sQuery(id+"F2.wireOp",EDGE,"E6.10.4.0")}),1.0]])]});
            var Q78;
            Q78=makeQuery(id+"F2.imprint","IMPRINT",FACE,{"disambiguationData":[TD([[makeQuery(id+"F2.imprint","IMPRINT",EDGE,{"derivedFrom":sQuery(id+"F2.wireOp",EDGE,"E16.MirrorC")}),-1.0]])]});
            var Q79;
            Q79=makeQuery(id+"F2.imprint","IMPRINT",FACE,{"disambiguationData":[TD([[makeQuery(id+"F2.imprint","IMPRINT",EDGE,{"derivedFrom":sQuery(id+"F2.wireOp",EDGE,"E206.MirrorC")}),-1.0]])]});
            var Q80;
            Q80=makeQuery(id+"F2.imprint","IMPRINT",FACE,{"disambiguationData":[TD([[makeQuery(id+"F2.imprint","IMPRINT",EDGE,{"derivedFrom":sQuery(id+"F2.wireOp",EDGE,"E222.MirrorC")}),-1.0]])]});
            var Q81;
            Q81=makeQuery(id+"F2.imprint","IMPRINT",FACE,{"disambiguationData":[TD([[makeQuery(id+"F2.imprint","IMPRINT",EDGE,{"derivedFrom":sQuery(id+"F2.wireOp",EDGE,"E153.MirrorC")}),-1.0]])]});
            var Q82;
            Q82=makeQuery(id+"F2.imprint","IMPRINT",FACE,{"disambiguationData":[TD([[makeQuery(id+"F2.imprint","IMPRINT",EDGE,{"derivedFrom":sQuery(id+"F2.wireOp",EDGE,"E168.MirrorC")}),1.0]])]});
            var Q83;
            Q83=makeQuery(id+"F2.imprint","IMPRINT",FACE,{"disambiguationData":[TD([[makeQuery(id+"F2.imprint","IMPRINT",EDGE,{"derivedFrom":sQuery(id+"F2.wireOp",EDGE,"E179.MirrorC")}),1.0]])]});
            var Q84;
            Q84=makeQuery(id+"F2.imprint","IMPRINT",FACE,{"disambiguationData":[TD([[makeQuery(id+"F2.imprint","IMPRINT",EDGE,{"derivedFrom":sQuery(id+"F2.wireOp",EDGE,"E193.MirrorC")}),-1.0]])]});
            var Q85;
            Q85=makeQuery(id+"F2.imprint","IMPRINT",FACE,{"disambiguationData":[TD([[makeQuery(id+"F2.imprint","IMPRINT",EDGE,{"derivedFrom":sQuery(id+"F2.wireOp",EDGE,"E6.0.5.0")}),-1.0]])]});
            var Q86;
            Q86=makeQuery(id+"F2.imprint","IMPRINT",FACE,{"disambiguationData":[TD([[makeQuery(id+"F2.imprint","IMPRINT",EDGE,{"derivedFrom":sQuery(id+"F2.wireOp",EDGE,"E45.MirrorC")}),-1.0]])]});
            var Q87;
            Q87=makeQuery(id+"F2.imprint","IMPRINT",FACE,{"disambiguationData":[TD([[makeQuery(id+"F2.imprint","IMPRINT",EDGE,{"derivedFrom":sQuery(id+"F2.wireOp",EDGE,"E63.MirrorC")}),-1.0]])]});
            var Q88;
            Q88=makeQuery(id+"F2.imprint","IMPRINT",FACE,{"disambiguationData":[TD([[makeQuery(id+"F2.imprint","IMPRINT",EDGE,{"derivedFrom":sQuery(id+"F2.wireOp",EDGE,"E83.MirrorC")}),-1.0]])]});
            var Q89;
            Q89=makeQuery(id+"F2.imprint","IMPRINT",FACE,{"disambiguationData":[TD([[makeQuery(id+"F2.imprint","IMPRINT",EDGE,{"derivedFrom":sQuery(id+"F2.wireOp",EDGE,"E6.5.1.0")}),1.0]])]});
            var Q90;
            Q90=makeQuery(id+"F2.imprint","IMPRINT",FACE,{"disambiguationData":[TD([[makeQuery(id+"F2.imprint","IMPRINT",EDGE,{"derivedFrom":sQuery(id+"F2.wireOp",EDGE,"E6.7.5.0")}),1.0]])]});
            var Q91;
            Q91=makeQuery(id+"F2.imprint","IMPRINT",FACE,{"disambiguationData":[TD([[makeQuery(id+"F2.imprint","IMPRINT",EDGE,{"derivedFrom":sQuery(id+"F2.wireOp",EDGE,"E6.10.3.0")}),1.0]])]});
            var Q92;
            Q92=makeQuery(id+"F2.imprint","IMPRINT",FACE,{"disambiguationData":[TD([[makeQuery(id+"F2.imprint","IMPRINT",EDGE,{"derivedFrom":sQuery(id+"F2.wireOp",EDGE,"E15.MirrorC")}),-1.0]])]});
            var Q93;
            Q93=makeQuery(id+"F2.imprint","IMPRINT",FACE,{"disambiguationData":[TD([[makeQuery(id+"F2.imprint","IMPRINT",EDGE,{"derivedFrom":sQuery(id+"F2.wireOp",EDGE,"E205.MirrorC")}),-1.0]])]});
            var Q94;
            Q94=makeQuery(id+"F2.imprint","IMPRINT",FACE,{"disambiguationData":[TD([[makeQuery(id+"F2.imprint","IMPRINT",EDGE,{"derivedFrom":sQuery(id+"F2.wireOp",EDGE,"E221.MirrorC")}),1.0]])]});
            var Q95;
            Q95=makeQuery(id+"F2.imprint","IMPRINT",FACE,{"disambiguationData":[TD([[makeQuery(id+"F2.imprint","IMPRINT",EDGE,{"derivedFrom":sQuery(id+"F2.wireOp",EDGE,"E152.MirrorC")}),-1.0]])]});
            var Q96;
            Q96=makeQuery(id+"F2.imprint","IMPRINT",FACE,{"disambiguationData":[TD([[makeQuery(id+"F2.imprint","IMPRINT",EDGE,{"derivedFrom":sQuery(id+"F2.wireOp",EDGE,"E6.7.0.0")}),-1.0]])]});
            var Q97;
            Q97=makeQuery(id+"F2.imprint","IMPRINT",FACE,{"disambiguationData":[TD([[makeQuery(id+"F2.imprint","IMPRINT",EDGE,{"derivedFrom":sQuery(id+"F2.wireOp",EDGE,"E178.MirrorC")}),1.0]])]});
            var Q98;
            Q98=makeQuery(id+"F2.imprint","IMPRINT",FACE,{"disambiguationData":[TD([[makeQuery(id+"F2.imprint","IMPRINT",EDGE,{"derivedFrom":sQuery(id+"F2.wireOp",EDGE,"E192.MirrorC")}),1.0]])]});
            var Q99;
            Q99=makeQuery(id+"F2.imprint","IMPRINT",FACE,{"disambiguationData":[TD([[makeQuery(id+"F2.imprint","IMPRINT",EDGE,{"derivedFrom":sQuery(id+"F2.wireOp",EDGE,"E103.MirrorC")}),1.0]])]});
            var Q100;
            Q100=makeQuery(id+"F2.imprint","IMPRINT",FACE,{"disambiguationData":[TD([[makeQuery(id+"F2.imprint","IMPRINT",EDGE,{"derivedFrom":sQuery(id+"F2.wireOp",EDGE,"E87.MirrorC")}),-1.0]])]});
            var Q101;
            Q101=makeQuery(id+"F2.imprint","IMPRINT",FACE,{"disambiguationData":[TD([[makeQuery(id+"F2.imprint","IMPRINT",EDGE,{"derivedFrom":sQuery(id+"F2.wireOp",EDGE,"E124.MirrorC")}),1.0]])]});
            var Q102;
            Q102=makeQuery(id+"F2.imprint","IMPRINT",FACE,{"disambiguationData":[TD([[makeQuery(id+"F2.imprint","IMPRINT",EDGE,{"derivedFrom":sQuery(id+"F2.wireOp",EDGE,"E138.MirrorC")}),-1.0]])]});
            var Q103;
            Q103=makeQuery(id+"F2.imprint","IMPRINT",FACE,{"disambiguationData":[TD([[makeQuery(id+"F2.imprint","IMPRINT",EDGE,{"derivedFrom":sQuery(id+"F2.wireOp",EDGE,"E6.4.6.0")}),1.0]])]});
            var Q104;
            Q104=makeQuery(id+"F2.imprint","IMPRINT",FACE,{"disambiguationData":[TD([[makeQuery(id+"F2.imprint","IMPRINT",EDGE,{"derivedFrom":sQuery(id+"F2.wireOp",EDGE,"E6.7.4.0")}),1.0]])]});
            var Q105;
            Q105=makeQuery(id+"F2.imprint","IMPRINT",FACE,{"disambiguationData":[TD([[makeQuery(id+"F2.imprint","IMPRINT",EDGE,{"derivedFrom":sQuery(id+"F2.wireOp",EDGE,"E6.10.2.0")}),1.0]])]});
            var Q106;
            Q106=makeQuery(id+"F2.imprint","IMPRINT",FACE,{"disambiguationData":[TD([[makeQuery(id+"F2.imprint","IMPRINT",EDGE,{"derivedFrom":sQuery(id+"F2.wireOp",EDGE,"E14.MirrorC")}),-1.0]])]});
            var Q107;
            Q107=makeQuery(id+"F2.imprint","IMPRINT",FACE,{"disambiguationData":[TD([[makeQuery(id+"F2.imprint","IMPRINT",EDGE,{"derivedFrom":sQuery(id+"F2.wireOp",EDGE,"E204.MirrorC")}),1.0]])]});
            var Q108;
            Q108=makeQuery(id+"F2.imprint","IMPRINT",FACE,{"disambiguationData":[TD([[makeQuery(id+"F2.imprint","IMPRINT",EDGE,{"derivedFrom":sQuery(id+"F2.wireOp",EDGE,"E220.MirrorC")}),1.0]])]});
            var Q109;
            Q109=makeQuery(id+"F2.imprint","IMPRINT",FACE,{"disambiguationData":[TD([[makeQuery(id+"F2.imprint","IMPRINT",EDGE,{"derivedFrom":sQuery(id+"F2.wireOp",EDGE,"E151.MirrorC")}),-1.0]])]});
            var Q110;
            Q110=makeQuery(id+"F2.imprint","IMPRINT",FACE,{"disambiguationData":[TD([[makeQuery(id+"F2.imprint","IMPRINT",EDGE,{"derivedFrom":sQuery(id+"F2.wireOp",EDGE,"E167.MirrorC")}),-1.0]])]});
            var Q111;
            Q111=makeQuery(id+"F2.imprint","IMPRINT",FACE,{"disambiguationData":[TD([[makeQuery(id+"F2.imprint","IMPRINT",EDGE,{"derivedFrom":sQuery(id+"F2.wireOp",EDGE,"E54.MirrorC")}),1.0]])]});
            var Q112;
            Q112=makeQuery(id+"F2.imprint","IMPRINT",FACE,{"disambiguationData":[TD([[makeQuery(id+"F2.imprint","IMPRINT",EDGE,{"derivedFrom":sQuery(id+"F2.wireOp",EDGE,"E191.MirrorC")}),-1.0]])]});
            var Q113;
            Q113=makeQuery(id+"F2.imprint","IMPRINT",FACE,{"disambiguationData":[TD([[makeQuery(id+"F2.imprint","IMPRINT",EDGE,{"derivedFrom":sQuery(id+"F2.wireOp",EDGE,"E102.MirrorC")}),1.0]])]});
            var Q114;
            Q114=makeQuery(id+"F2.imprint","IMPRINT",FACE,{"disambiguationData":[TD([[makeQuery(id+"F2.imprint","IMPRINT",EDGE,{"derivedFrom":sQuery(id+"F2.wireOp",EDGE,"E91.MirrorC")}),-1.0]])]});
            var Q115;
            Q115=makeQuery(id+"F2.imprint","IMPRINT",FACE,{"disambiguationData":[TD([[makeQuery(id+"F2.imprint","IMPRINT",EDGE,{"derivedFrom":sQuery(id+"F2.wireOp",EDGE,"E123.MirrorC")}),1.0]])]});
            var Q116;
            Q116=makeQuery(id+"F2.imprint","IMPRINT",FACE,{"disambiguationData":[TD([[makeQuery(id+"F2.imprint","IMPRINT",EDGE,{"derivedFrom":sQuery(id+"F2.wireOp",EDGE,"E137.MirrorC")}),1.0]])]});
            var Q117;
            Q117=makeQuery(id+"F2.imprint","IMPRINT",FACE,{"disambiguationData":[TD([[makeQuery(id+"F2.imprint","IMPRINT",EDGE,{"derivedFrom":sQuery(id+"F2.wireOp",EDGE,"E6.0.6.0")}),-1.0]])]});
            var Q118;
            Q118=makeQuery(id+"F2.imprint","IMPRINT",FACE,{"disambiguationData":[TD([[makeQuery(id+"F2.imprint","IMPRINT",EDGE,{"derivedFrom":sQuery(id+"F2.wireOp",EDGE,"E44.MirrorC")}),-1.0]])]});
            var Q119;
            Q119=makeQuery(id+"F2.imprint","IMPRINT",FACE,{"disambiguationData":[TD([[makeQuery(id+"F2.imprint","IMPRINT",EDGE,{"derivedFrom":sQuery(id+"F2.wireOp",EDGE,"E62.MirrorC")}),-1.0]])]});
            var Q120;
            Q120=makeQuery(id+"F2.imprint","IMPRINT",FACE,{"disambiguationData":[TD([[makeQuery(id+"F2.imprint","IMPRINT",EDGE,{"derivedFrom":sQuery(id+"F2.wireOp",EDGE,"E82.MirrorC")}),-1.0]])]});
            var Q121;
            Q121=makeQuery(id+"F2.imprint","IMPRINT",FACE,{"disambiguationData":[TD([[makeQuery(id+"F2.imprint","IMPRINT",EDGE,{"derivedFrom":sQuery(id+"F2.wireOp",EDGE,"E203.MirrorC")}),-1.0]])]});
            var Q122;
            Q122=makeQuery(id+"F2.imprint","IMPRINT",FACE,{"disambiguationData":[TD([[makeQuery(id+"F2.imprint","IMPRINT",EDGE,{"derivedFrom":sQuery(id+"F2.wireOp",EDGE,"E219.MirrorC")}),1.0]])]});
            var Q123;
            Q123=makeQuery(id+"F2.imprint","IMPRINT",FACE,{"disambiguationData":[TD([[makeQuery(id+"F2.imprint","IMPRINT",EDGE,{"derivedFrom":sQuery(id+"F2.wireOp",EDGE,"E150.MirrorC")}),-1.0]])]});
            var Q124;
            Q124=makeQuery(id+"F2.imprint","IMPRINT",FACE,{"disambiguationData":[TD([[makeQuery(id+"F2.imprint","IMPRINT",EDGE,{"derivedFrom":sQuery(id+"F2.wireOp",EDGE,"E166.MirrorC")}),-1.0]])]});
            var Q125;
            Q125=makeQuery(id+"F2.imprint","IMPRINT",FACE,{"disambiguationData":[TD([[makeQuery(id+"F2.imprint","IMPRINT",EDGE,{"derivedFrom":sQuery(id+"F2.wireOp",EDGE,"E6.4.0.0")}),-1.0]])]});
            var Q126;
            Q126=makeQuery(id+"F2.imprint","IMPRINT",FACE,{"disambiguationData":[TD([[makeQuery(id+"F2.imprint","IMPRINT",EDGE,{"derivedFrom":sQuery(id+"F2.wireOp",EDGE,"E190.MirrorC")}),-1.0]])]});
            var Q127;
            Q127=makeQuery(id+"F2.imprint","IMPRINT",FACE,{"disambiguationData":[TD([[makeQuery(id+"F2.imprint","IMPRINT",EDGE,{"derivedFrom":sQuery(id+"F2.wireOp",EDGE,"E101.MirrorC")}),1.0]])]});
            var Q128;
            Q128=makeQuery(id+"F2.imprint","IMPRINT",FACE,{"disambiguationData":[TD([[makeQuery(id+"F2.imprint","IMPRINT",EDGE,{"derivedFrom":sQuery(id+"F2.wireOp",EDGE,"E89.MirrorC")}),-1.0]])]});
            var Q129;
            Q129=makeQuery(id+"F2.imprint","IMPRINT",FACE,{"disambiguationData":[TD([[makeQuery(id+"F2.imprint","IMPRINT",EDGE,{"derivedFrom":sQuery(id+"F2.wireOp",EDGE,"E122.MirrorC")}),-1.0]])]});
            var Q130;
            Q130=makeQuery(id+"F2.imprint","IMPRINT",FACE,{"disambiguationData":[TD([[makeQuery(id+"F2.imprint","IMPRINT",EDGE,{"derivedFrom":sQuery(id+"F2.wireOp",EDGE,"E136.MirrorC")}),1.0]])]});
            var Q131;
            Q131=makeQuery(id+"F2.imprint","IMPRINT",FACE,{"disambiguationData":[TD([[makeQuery(id+"F2.imprint","IMPRINT",EDGE,{"derivedFrom":sQuery(id+"F2.wireOp",EDGE,"E29.MirrorC")}),-1.0]])]});
            var Q132;
            Q132=makeQuery(id+"F2.imprint","IMPRINT",FACE,{"disambiguationData":[TD([[makeQuery(id+"F2.imprint","IMPRINT",EDGE,{"derivedFrom":sQuery(id+"F2.wireOp",EDGE,"E43.MirrorC")}),-1.0]])]});
            var Q133;
            Q133=makeQuery(id+"F2.imprint","IMPRINT",FACE,{"disambiguationData":[TD([[makeQuery(id+"F2.imprint","IMPRINT",EDGE,{"derivedFrom":sQuery(id+"F2.wireOp",EDGE,"E61.MirrorC")}),-1.0]])]});
            var Q134;
            Q134=makeQuery(id+"F2.imprint","IMPRINT",FACE,{"disambiguationData":[TD([[makeQuery(id+"F2.imprint","IMPRINT",EDGE,{"derivedFrom":sQuery(id+"F2.wireOp",EDGE,"E81.MirrorC")}),-1.0]])]});
            var Q135;
            Q135=makeQuery(id+"F2.imprint","IMPRINT",FACE,{"disambiguationData":[TD([[makeQuery(id+"F2.imprint","IMPRINT",EDGE,{"derivedFrom":sQuery(id+"F2.wireOp",EDGE,"E6.4.5.0")}),1.0]])]});
            var Q136;
            Q136=makeQuery(id+"F2.imprint","IMPRINT",FACE,{"disambiguationData":[TD([[makeQuery(id+"F2.imprint","IMPRINT",EDGE,{"derivedFrom":sQuery(id+"F2.wireOp",EDGE,"E6.7.3.0")}),1.0]])]});
            var Q137;
            Q137=makeQuery(id+"F2.imprint","IMPRINT",FACE,{"disambiguationData":[TD([[makeQuery(id+"F2.imprint","IMPRINT",EDGE,{"derivedFrom":sQuery(id+"F2.wireOp",EDGE,"E6.10.1.0")}),1.0]])]});
            var Q138;
            Q138=makeQuery(id+"F2.imprint","IMPRINT",FACE,{"disambiguationData":[TD([[makeQuery(id+"F2.imprint","IMPRINT",EDGE,{"derivedFrom":sQuery(id+"F2.wireOp",EDGE,"E12.MirrorC")}),-1.0]])]});
            var Q139;
            Q139=makeQuery(id+"F2.imprint","IMPRINT",FACE,{"disambiguationData":[TD([[makeQuery(id+"F2.imprint","IMPRINT",EDGE,{"derivedFrom":sQuery(id+"F2.wireOp",EDGE,"E177.MirrorC")}),-1.0]])]});
            var Q140;
            Q140=makeQuery(id+"F2.imprint","IMPRINT",FACE,{"disambiguationData":[TD([[makeQuery(id+"F2.imprint","IMPRINT",EDGE,{"derivedFrom":sQuery(id+"F2.wireOp",EDGE,"E189.MirrorC")}),-1.0]])]});
            var Q141;
            Q141=makeQuery(id+"F2.imprint","IMPRINT",FACE,{"disambiguationData":[TD([[makeQuery(id+"F2.imprint","IMPRINT",EDGE,{"derivedFrom":sQuery(id+"F2.wireOp",EDGE,"E202.MirrorC")}),-1.0]])]});
            var Q142;
            Q142=makeQuery(id+"F2.imprint","IMPRINT",FACE,{"disambiguationData":[TD([[makeQuery(id+"F2.imprint","IMPRINT",EDGE,{"derivedFrom":sQuery(id+"F2.wireOp",EDGE,"E218.MirrorC")}),-1.0]])]});
            var Q143;
            Q143=makeQuery(id+"F2.imprint","IMPRINT",FACE,{"disambiguationData":[TD([[makeQuery(id+"F2.imprint","IMPRINT",EDGE,{"derivedFrom":sQuery(id+"F2.wireOp",EDGE,"E6.8.0.0")}),-1.0]])]});
            var Q144;
            Q144=makeQuery(id+"F2.imprint","IMPRINT",FACE,{"disambiguationData":[TD([[makeQuery(id+"F2.imprint","IMPRINT",EDGE,{"derivedFrom":sQuery(id+"F2.wireOp",EDGE,"E6.10.0.0")}),-1.0]])]});
            var Q145;
            Q145=makeQuery(id+"F2.imprint","IMPRINT",FACE,{"disambiguationData":[TD([[makeQuery(id+"F2.imprint","IMPRINT",EDGE,{"derivedFrom":sQuery(id+"F2.wireOp",EDGE,"E77.MirrorC")}),1.0]])]});
            var Q146;
            Q146=makeQuery(id+"F2.imprint","IMPRINT",FACE,{"disambiguationData":[TD([[makeQuery(id+"F2.imprint","IMPRINT",EDGE,{"derivedFrom":sQuery(id+"F2.wireOp",EDGE,"E165.MirrorC")}),-1.0]])]});
            var Q147;
            Q147=makeQuery(id+"F2.imprint","IMPRINT",FACE,{"disambiguationData":[TD([[makeQuery(id+"F2.imprint","IMPRINT",EDGE,{"derivedFrom":sQuery(id+"F2.wireOp",EDGE,"E60.MirrorC")}),-1.0]])]});
            var Q148;
            Q148=makeQuery(id+"F2.imprint","IMPRINT",FACE,{"disambiguationData":[TD([[makeQuery(id+"F2.imprint","IMPRINT",EDGE,{"derivedFrom":sQuery(id+"F2.wireOp",EDGE,"E80.MirrorC")}),-1.0]])]});
            var Q149;
            Q149=makeQuery(id+"F2.imprint","IMPRINT",FACE,{"disambiguationData":[TD([[makeQuery(id+"F2.imprint","IMPRINT",EDGE,{"derivedFrom":sQuery(id+"F2.wireOp",EDGE,"E100.MirrorC")}),1.0]])]});
            var Q150;
            Q150=makeQuery(id+"F2.imprint","IMPRINT",FACE,{"disambiguationData":[TD([[makeQuery(id+"F2.imprint","IMPRINT",EDGE,{"derivedFrom":sQuery(id+"F2.wireOp",EDGE,"E88.MirrorC")}),-1.0]])]});
            var Q151;
            Q151=makeQuery(id+"F2.imprint","IMPRINT",FACE,{"disambiguationData":[TD([[makeQuery(id+"F2.imprint","IMPRINT",EDGE,{"derivedFrom":sQuery(id+"F2.wireOp",EDGE,"E6.9.6.0")}),1.0]])]});
            var Q152;
            Q152=makeQuery(id+"F2.imprint","IMPRINT",FACE,{"disambiguationData":[TD([[makeQuery(id+"F2.imprint","IMPRINT",EDGE,{"derivedFrom":sQuery(id+"F2.wireOp",EDGE,"E10.MirrorC")}),-1.0]])]});
            var Q153;
            Q153=makeQuery(id+"F2.imprint","IMPRINT",FACE,{"disambiguationData":[TD([[makeQuery(id+"F2.imprint","IMPRINT",EDGE,{"derivedFrom":sQuery(id+"F2.wireOp",EDGE,"E28.MirrorC")}),-1.0]])]});
            var Q154;
            Q154=makeQuery(id+"F2.imprint","IMPRINT",FACE,{"disambiguationData":[TD([[makeQuery(id+"F2.imprint","IMPRINT",EDGE,{"derivedFrom":sQuery(id+"F2.wireOp",EDGE,"E42.MirrorC")}),-1.0]])]});
            var Q155;
            Q155=makeQuery(id+"F2.imprint","IMPRINT",FACE,{"disambiguationData":[TD([[makeQuery(id+"F2.imprint","IMPRINT",EDGE,{"derivedFrom":sQuery(id+"F2.wireOp",EDGE,"E6.4.4.0")}),1.0]])]});
            var Q156;
            Q156=makeQuery(id+"F2.imprint","IMPRINT",FACE,{"disambiguationData":[TD([[makeQuery(id+"F2.imprint","IMPRINT",EDGE,{"derivedFrom":sQuery(id+"F2.wireOp",EDGE,"E6.7.2.0")}),1.0]])]});
            var Q157;
            Q157=makeQuery(id+"F2.imprint","IMPRINT",FACE,{"disambiguationData":[TD([[makeQuery(id+"F2.imprint","IMPRINT",EDGE,{"derivedFrom":sQuery(id+"F2.wireOp",EDGE,"E176.MirrorC")}),-1.0]])]});
            var Q158;
            Q158=makeQuery(id+"F2.imprint","IMPRINT",FACE,{"disambiguationData":[TD([[makeQuery(id+"F2.imprint","IMPRINT",EDGE,{"derivedFrom":sQuery(id+"F2.wireOp",EDGE,"E188.MirrorC")}),1.0]])]});
            var Q159;
            Q159=makeQuery(id+"F2.imprint","IMPRINT",FACE,{"disambiguationData":[TD([[makeQuery(id+"F2.imprint","IMPRINT",EDGE,{"derivedFrom":sQuery(id+"F2.wireOp",EDGE,"E201.MirrorC")}),1.0]])]});
            var Q160;
            Q160=makeQuery(id+"F2.imprint","IMPRINT",FACE,{"disambiguationData":[TD([[makeQuery(id+"F2.imprint","IMPRINT",EDGE,{"derivedFrom":sQuery(id+"F2.wireOp",EDGE,"E217.MirrorC")}),-1.0]])]});
            var Q161;
            Q161=makeQuery(id+"F2.imprint","IMPRINT",FACE,{"disambiguationData":[TD([[makeQuery(id+"F2.imprint","IMPRINT",EDGE,{"derivedFrom":sQuery(id+"F2.wireOp",EDGE,"E121.MirrorC")}),-1.0]])]});
            var Q162;
            Q162=makeQuery(id+"F2.imprint","IMPRINT",FACE,{"disambiguationData":[TD([[makeQuery(id+"F2.imprint","IMPRINT",EDGE,{"derivedFrom":sQuery(id+"F2.wireOp",EDGE,"E135.MirrorC")}),-1.0]])]});
            var Q163;
            Q163=makeQuery(id+"F2.imprint","IMPRINT",FACE,{"disambiguationData":[TD([[makeQuery(id+"F2.imprint","IMPRINT",EDGE,{"derivedFrom":sQuery(id+"F2.wireOp",EDGE,"E149.MirrorC")}),1.0]])]});
            var Q164;
            Q164=makeQuery(id+"F2.imprint","IMPRINT",FACE,{"disambiguationData":[TD([[makeQuery(id+"F2.imprint","IMPRINT",EDGE,{"derivedFrom":sQuery(id+"F2.wireOp",EDGE,"E164.MirrorC")}),1.0]])]});
            var Q165;
            Q165=makeQuery(id+"F2.imprint","IMPRINT",FACE,{"disambiguationData":[TD([[makeQuery(id+"F2.imprint","IMPRINT",EDGE,{"derivedFrom":sQuery(id+"F2.wireOp",EDGE,"E59.MirrorC")}),-1.0]])]});
            var Q166;
            Q166=makeQuery(id+"F2.imprint","IMPRINT",FACE,{"disambiguationData":[TD([[makeQuery(id+"F2.imprint","IMPRINT",EDGE,{"derivedFrom":sQuery(id+"F2.wireOp",EDGE,"E79.MirrorC")}),-1.0]])]});
            var Q167;
            Q167=makeQuery(id+"F2.imprint","IMPRINT",FACE,{"disambiguationData":[TD([[makeQuery(id+"F2.imprint","IMPRINT",EDGE,{"derivedFrom":sQuery(id+"F2.wireOp",EDGE,"E66.MirrorC")}),1.0]])]});
            var Q168;
            Q168=makeQuery(id+"F2.imprint","IMPRINT",FACE,{"disambiguationData":[TD([[makeQuery(id+"F2.imprint","IMPRINT",EDGE,{"derivedFrom":sQuery(id+"F2.wireOp",EDGE,"E86.MirrorC")}),-1.0]])]});
            var Q169;
            Q169=makeQuery(id+"F2.imprint","IMPRINT",FACE,{"disambiguationData":[TD([[makeQuery(id+"F2.imprint","IMPRINT",EDGE,{"derivedFrom":sQuery(id+"F2.wireOp",EDGE,"E6.9.5.0")}),1.0]])]});
            var Q170;
            Q170=makeQuery(id+"F2.imprint","IMPRINT",FACE,{"disambiguationData":[TD([[makeQuery(id+"F2.imprint","IMPRINT",EDGE,{"derivedFrom":sQuery(id+"F2.wireOp",EDGE,"E9.MirrorC")}),-1.0]])]});
            var Q171;
            Q171=makeQuery(id+"F2.imprint","IMPRINT",FACE,{"disambiguationData":[TD([[makeQuery(id+"F2.imprint","IMPRINT",EDGE,{"derivedFrom":sQuery(id+"F2.wireOp",EDGE,"E27.MirrorC")}),-1.0]])]});
            var Q172;
            Q172=makeQuery(id+"F2.imprint","IMPRINT",FACE,{"disambiguationData":[TD([[makeQuery(id+"F2.imprint","IMPRINT",EDGE,{"derivedFrom":sQuery(id+"F2.wireOp",EDGE,"E40.MirrorC")}),-1.0]])]});
            var Q173;
            Q173=makeQuery(id+"F2.imprint","IMPRINT",FACE,{"disambiguationData":[TD([[makeQuery(id+"F2.imprint","IMPRINT",EDGE,{"derivedFrom":sQuery(id+"F2.wireOp",EDGE,"E6.4.3.0")}),1.0]])]});
            var Q174;
            Q174=makeQuery(id+"F2.imprint","IMPRINT",FACE,{"disambiguationData":[TD([[makeQuery(id+"F2.imprint","IMPRINT",EDGE,{"derivedFrom":sQuery(id+"F2.wireOp",EDGE,"E6.7.1.0")}),1.0]])]});
            var Q175;
            Q175=makeQuery(id+"F2.imprint","IMPRINT",FACE,{"disambiguationData":[TD([[makeQuery(id+"F2.imprint","IMPRINT",EDGE,{"derivedFrom":sQuery(id+"F2.wireOp",EDGE,"E175.MirrorC")}),-1.0]])]});
            var Q176;
            Q176=makeQuery(id+"F2.imprint","IMPRINT",FACE,{"disambiguationData":[TD([[makeQuery(id+"F2.imprint","IMPRINT",EDGE,{"derivedFrom":sQuery(id+"F2.wireOp",EDGE,"E187.MirrorC")}),1.0]])]});
            var Q177;
            Q177=makeQuery(id+"F2.imprint","IMPRINT",FACE,{"disambiguationData":[TD([[makeQuery(id+"F2.imprint","IMPRINT",EDGE,{"derivedFrom":sQuery(id+"F2.wireOp",EDGE,"E6.5.0.0")}),-1.0]])]});
            var Q178;
            Q178=makeQuery(id+"F2.imprint","IMPRINT",FACE,{"disambiguationData":[TD([[makeQuery(id+"F2.imprint","IMPRINT",EDGE,{"derivedFrom":sQuery(id+"F2.wireOp",EDGE,"E216.MirrorC")}),-1.0]])]});
            var Q179;
            Q179=makeQuery(id+"F2.imprint","IMPRINT",FACE,{"disambiguationData":[TD([[makeQuery(id+"F2.imprint","IMPRINT",EDGE,{"derivedFrom":sQuery(id+"F2.wireOp",EDGE,"E120.MirrorC")}),-1.0]])]});
            var Q180;
            Q180=makeQuery(id+"F2.imprint","IMPRINT",FACE,{"disambiguationData":[TD([[makeQuery(id+"F2.imprint","IMPRINT",EDGE,{"derivedFrom":sQuery(id+"F2.wireOp",EDGE,"E134.MirrorC")}),1.0]])]});
            var Q181;
            Q181=makeQuery(id+"F2.imprint","IMPRINT",FACE,{"disambiguationData":[TD([[makeQuery(id+"F2.imprint","IMPRINT",EDGE,{"derivedFrom":sQuery(id+"F2.wireOp",EDGE,"E148.MirrorC")}),1.0]])]});
            var Q182;
            Q182=makeQuery(id+"F2.imprint","IMPRINT",FACE,{"disambiguationData":[TD([[makeQuery(id+"F2.imprint","IMPRINT",EDGE,{"derivedFrom":sQuery(id+"F2.wireOp",EDGE,"E163.MirrorC")}),1.0]])]});
            var Q183;
            Q183=makeQuery(id+"F2.imprint","IMPRINT",FACE,{"disambiguationData":[TD([[makeQuery(id+"F2.imprint","IMPRINT",EDGE,{"derivedFrom":sQuery(id+"F2.wireOp",EDGE,"E58.MirrorC")}),-1.0]])]});
            var Q184;
            Q184=makeQuery(id+"F2.imprint","IMPRINT",FACE,{"disambiguationData":[TD([[makeQuery(id+"F2.imprint","IMPRINT",EDGE,{"derivedFrom":sQuery(id+"F2.wireOp",EDGE,"E78.MirrorC")}),-1.0]])]});
            var Q185;
            Q185=makeQuery(id+"F2.imprint","IMPRINT",FACE,{"disambiguationData":[TD([[makeQuery(id+"F2.imprint","IMPRINT",EDGE,{"derivedFrom":sQuery(id+"F2.wireOp",EDGE,"E99.MirrorC")}),-1.0]])]});
            var Q186;
            Q186=makeQuery(id+"F2.imprint","IMPRINT",FACE,{"disambiguationData":[TD([[makeQuery(id+"F2.imprint","IMPRINT",EDGE,{"derivedFrom":sQuery(id+"F2.wireOp",EDGE,"E6.1.0.0")}),-1.0]])]});
            var Q187;
            Q187=makeQuery(id+"F2.imprint","IMPRINT",FACE,{"disambiguationData":[TD([[makeQuery(id+"F2.imprint","IMPRINT",EDGE,{"derivedFrom":sQuery(id+"F2.wireOp",EDGE,"E6.9.4.0")}),1.0]])]});
            var Q188;
            Q188=makeQuery(id+"F2.imprint","IMPRINT",FACE,{"disambiguationData":[TD([[makeQuery(id+"F2.imprint","IMPRINT",EDGE,{"derivedFrom":sQuery(id+"F2.wireOp",EDGE,"E8.MirrorC")}),-1.0]])]});
            var Q189;
            Q189=makeQuery(id+"F2.imprint","IMPRINT",FACE,{"disambiguationData":[TD([[makeQuery(id+"F2.imprint","IMPRINT",EDGE,{"derivedFrom":sQuery(id+"F2.wireOp",EDGE,"E26.MirrorC")}),-1.0]])]});
            var Q190;
            Q190=makeQuery(id+"F2.imprint","IMPRINT",FACE,{"disambiguationData":[TD([[makeQuery(id+"F2.imprint","IMPRINT",EDGE,{"derivedFrom":sQuery(id+"F2.wireOp",EDGE,"E39.MirrorC")}),-1.0]])]});
            var Q191;
            Q191=makeQuery(id+"F2.imprint","IMPRINT",FACE,{"disambiguationData":[TD([[makeQuery(id+"F2.imprint","IMPRINT",EDGE,{"derivedFrom":sQuery(id+"F2.wireOp",EDGE,"E6.4.2.0")}),1.0]])]});
            var Q192;
            Q192=makeQuery(id+"F2.imprint","IMPRINT",FACE,{"disambiguationData":[TD([[makeQuery(id+"F2.imprint","IMPRINT",EDGE,{"derivedFrom":sQuery(id+"F2.wireOp",EDGE,"E6.6.6.0")}),1.0]])]});
            var Q193;
            Q193=makeQuery(id+"F2.imprint","IMPRINT",FACE,{"disambiguationData":[TD([[makeQuery(id+"F2.imprint","IMPRINT",EDGE,{"derivedFrom":sQuery(id+"F2.wireOp",EDGE,"E30.MirrorC")}),1.0]])]});
            var Q194;
            Q194=makeQuery(id+"F2.imprint","IMPRINT",FACE,{"disambiguationData":[TD([[makeQuery(id+"F2.imprint","IMPRINT",EDGE,{"derivedFrom":sQuery(id+"F2.wireOp",EDGE,"E186.MirrorC")}),1.0]])]});
            var Q195;
            Q195=makeQuery(id+"F2.imprint","IMPRINT",FACE,{"disambiguationData":[TD([[makeQuery(id+"F2.imprint","IMPRINT",EDGE,{"derivedFrom":sQuery(id+"F2.wireOp",EDGE,"E41.MirrorC")}),1.0]])]});
            var Q196;
            Q196=makeQuery(id+"F2.imprint","IMPRINT",FACE,{"disambiguationData":[TD([[makeQuery(id+"F2.imprint","IMPRINT",EDGE,{"derivedFrom":sQuery(id+"F2.wireOp",EDGE,"E215.MirrorC")}),1.0]])]});
            var Q197;
            Q197=makeQuery(id+"F2.imprint","IMPRINT",FACE,{"disambiguationData":[TD([[makeQuery(id+"F2.imprint","IMPRINT",EDGE,{"derivedFrom":sQuery(id+"F2.wireOp",EDGE,"E119.MirrorC")}),1.0]])]});
            var Q198;
            Q198=makeQuery(id+"F2.imprint","IMPRINT",FACE,{"disambiguationData":[TD([[makeQuery(id+"F2.imprint","IMPRINT",EDGE,{"derivedFrom":sQuery(id+"F2.wireOp",EDGE,"E133.MirrorC")}),1.0]])]});
            var Q199;
            Q199=makeQuery(id+"F2.imprint","IMPRINT",FACE,{"disambiguationData":[TD([[makeQuery(id+"F2.imprint","IMPRINT",EDGE,{"derivedFrom":sQuery(id+"F2.wireOp",EDGE,"E147.MirrorC")}),-1.0]])]});
            var Q200;
            Q200=makeQuery(id+"F2.imprint","IMPRINT",FACE,{"disambiguationData":[TD([[makeQuery(id+"F2.imprint","IMPRINT",EDGE,{"derivedFrom":sQuery(id+"F2.wireOp",EDGE,"E162.MirrorC")}),1.0]])]});
            var Q201;
            Q201=makeQuery(id+"F2.imprint","IMPRINT",FACE,{"disambiguationData":[TD([[makeQuery(id+"F2.imprint","IMPRINT",EDGE,{"derivedFrom":sQuery(id+"F2.wireOp",EDGE,"E57.MirrorC")}),-1.0]])]});
            var Q202;
            Q202=makeQuery(id+"F2.imprint","IMPRINT",FACE,{"disambiguationData":[TD([[makeQuery(id+"F2.imprint","IMPRINT",EDGE,{"derivedFrom":sQuery(id+"F2.wireOp",EDGE,"E76.MirrorC")}),-1.0]])]});
            var Q203;
            Q203=makeQuery(id+"F2.imprint","IMPRINT",FACE,{"disambiguationData":[TD([[makeQuery(id+"F2.imprint","IMPRINT",EDGE,{"derivedFrom":sQuery(id+"F2.wireOp",EDGE,"E98.MirrorC")}),-1.0]])]});
            var Q204;
            Q204=makeQuery(id+"F2.imprint","IMPRINT",FACE,{"disambiguationData":[TD([[makeQuery(id+"F2.imprint","IMPRINT",EDGE,{"derivedFrom":sQuery(id+"F2.wireOp",EDGE,"E113.MirrorC")}),-1.0]])]});
            var Q205;
            Q205=makeQuery(id+"F2.imprint","IMPRINT",FACE,{"disambiguationData":[TD([[makeQuery(id+"F2.imprint","IMPRINT",EDGE,{"derivedFrom":sQuery(id+"F2.wireOp",EDGE,"E6.9.3.0")}),1.0]])]});
            var Q206;
            Q206=makeQuery(id+"F2.imprint","IMPRINT",FACE,{"disambiguationData":[TD([[makeQuery(id+"F2.imprint","IMPRINT",EDGE,{"derivedFrom":sQuery(id+"F2.wireOp",EDGE,"E7.MirrorC")}),-1.0]])]});
            var Q207;
            Q207=makeQuery(id+"F2.imprint","IMPRINT",FACE,{"disambiguationData":[TD([[makeQuery(id+"F2.imprint","IMPRINT",EDGE,{"derivedFrom":sQuery(id+"F2.wireOp",EDGE,"E25.MirrorC")}),-1.0]])]});
            var Q208;
            Q208=makeQuery(id+"F2.imprint","IMPRINT",FACE,{"disambiguationData":[TD([[makeQuery(id+"F2.imprint","IMPRINT",EDGE,{"derivedFrom":sQuery(id+"F2.wireOp",EDGE,"E38.MirrorC")}),-1.0]])]});
            var Q209;
            Q209=makeQuery(id+"F2.imprint","IMPRINT",FACE,{"disambiguationData":[TD([[makeQuery(id+"F2.imprint","IMPRINT",EDGE,{"derivedFrom":sQuery(id+"F2.wireOp",EDGE,"E6.4.1.0")}),1.0]])]});
            var Q210;
            Q210=makeQuery(id+"F2.imprint","IMPRINT",FACE,{"disambiguationData":[TD([[makeQuery(id+"F2.imprint","IMPRINT",EDGE,{"derivedFrom":sQuery(id+"F2.wireOp",EDGE,"E6.6.5.0")}),1.0]])]});
            var Q211;
            Q211=makeQuery(id+"F2.imprint","IMPRINT",FACE,{"disambiguationData":[TD([[makeQuery(id+"F2.imprint","IMPRINT",EDGE,{"derivedFrom":sQuery(id+"F2.wireOp",EDGE,"E174.MirrorC")}),1.0]])]});
            var Q212;
            Q212=makeQuery(id+"F2.imprint","IMPRINT",FACE,{"disambiguationData":[TD([[makeQuery(id+"F2.imprint","IMPRINT",EDGE,{"derivedFrom":sQuery(id+"F2.wireOp",EDGE,"E185.MirrorC")}),1.0]])]});
            var Q213;
            Q213=makeQuery(id+"F2.imprint","IMPRINT",FACE,{"disambiguationData":[TD([[makeQuery(id+"F2.imprint","IMPRINT",EDGE,{"derivedFrom":sQuery(id+"F2.wireOp",EDGE,"E200.MirrorC")}),1.0]])]});
            var Q214;
            Q214=makeQuery(id+"F2.imprint","IMPRINT",FACE,{"disambiguationData":[TD([[makeQuery(id+"F2.imprint","IMPRINT",EDGE,{"derivedFrom":sQuery(id+"F2.wireOp",EDGE,"E214.MirrorC")}),1.0]])]});
            var Q215;
            Q215=makeQuery(id+"F2.imprint","IMPRINT",FACE,{"disambiguationData":[TD([[makeQuery(id+"F2.imprint","IMPRINT",EDGE,{"derivedFrom":sQuery(id+"F2.wireOp",EDGE,"E34.MirrorC")}),1.0]])]});
            var Q216;
            Q216=makeQuery(id+"F2.imprint","IMPRINT",FACE,{"disambiguationData":[TD([[makeQuery(id+"F2.imprint","IMPRINT",EDGE,{"derivedFrom":sQuery(id+"F2.wireOp",EDGE,"E132.MirrorC")}),1.0]])]});
            var Q217;
            Q217=makeQuery(id+"F2.imprint","IMPRINT",FACE,{"disambiguationData":[TD([[makeQuery(id+"F2.imprint","IMPRINT",EDGE,{"derivedFrom":sQuery(id+"F2.wireOp",EDGE,"E6.3.0.0")}),-1.0]])]});
            var Q218;
            Q218=makeQuery(id+"F2.imprint","IMPRINT",FACE,{"disambiguationData":[TD([[makeQuery(id+"F2.imprint","IMPRINT",EDGE,{"derivedFrom":sQuery(id+"F2.wireOp",EDGE,"E161.MirrorC")}),1.0]])]});
            var Q219;
            Q219=makeQuery(id+"F2.imprint","IMPRINT",FACE,{"disambiguationData":[TD([[makeQuery(id+"F2.imprint","IMPRINT",EDGE,{"derivedFrom":sQuery(id+"F2.wireOp",EDGE,"E56.MirrorC")}),-1.0]])]});
            var Q220;
            Q220=makeQuery(id+"F2.imprint","IMPRINT",FACE,{"disambiguationData":[TD([[makeQuery(id+"F2.imprint","IMPRINT",EDGE,{"derivedFrom":sQuery(id+"F2.wireOp",EDGE,"E75.MirrorC")}),-1.0]])]});
            var Q221;
            Q221=makeQuery(id+"F2.imprint","IMPRINT",FACE,{"disambiguationData":[TD([[makeQuery(id+"F2.imprint","IMPRINT",EDGE,{"derivedFrom":sQuery(id+"F2.wireOp",EDGE,"E6.6.0.0")}),-1.0]])]});
            var Q222;
            Q222=makeQuery(id+"F2.imprint","IMPRINT",FACE,{"disambiguationData":[TD([[makeQuery(id+"F2.imprint","IMPRINT",EDGE,{"derivedFrom":sQuery(id+"F2.wireOp",EDGE,"E112.MirrorC")}),-1.0]])]});
            var Q223;
            Q223=makeQuery(id+"F2.imprint","IMPRINT",FACE,{"disambiguationData":[TD([[makeQuery(id+"F2.imprint","IMPRINT",EDGE,{"derivedFrom":sQuery(id+"F2.wireOp",EDGE,"E6.9.2.0")}),1.0]])]});
            var Q224;
            Q224=makeQuery(id+"F2.imprint","IMPRINT",FACE,{"disambiguationData":[TD([[makeQuery(id+"F2.imprint","IMPRINT",EDGE,{"derivedFrom":sQuery(id+"F2.wireOp",EDGE,"E6.11.6.0")}),1.0]])]});
            var Q225;
            Q225=makeQuery(id+"F2.imprint","IMPRINT",FACE,{"disambiguationData":[TD([[makeQuery(id+"F2.imprint","IMPRINT",EDGE,{"derivedFrom":sQuery(id+"F2.wireOp",EDGE,"E24.MirrorC")}),-1.0]])]});
            var Q226;
            Q226=makeQuery(id+"F2.imprint","IMPRINT",FACE,{"disambiguationData":[TD([[makeQuery(id+"F2.imprint","IMPRINT",EDGE,{"derivedFrom":sQuery(id+"F2.wireOp",EDGE,"E37.MirrorC")}),-1.0]])]});
            var Q227;
            Q227=makeQuery(id+"F2.imprint","IMPRINT",FACE,{"disambiguationData":[TD([[makeQuery(id+"F2.imprint","IMPRINT",EDGE,{"derivedFrom":sQuery(id+"F2.wireOp",EDGE,"E6.3.6.0")}),1.0]])]});
            var Q228;
            Q228=makeQuery(id+"F2.imprint","IMPRINT",FACE,{"disambiguationData":[TD([[makeQuery(id+"F2.imprint","IMPRINT",EDGE,{"derivedFrom":sQuery(id+"F2.wireOp",EDGE,"E6.6.4.0")}),1.0]])]});
            var Q229;
            Q229=makeQuery(id+"F2.imprint","IMPRINT",FACE,{"disambiguationData":[TD([[makeQuery(id+"F2.imprint","IMPRINT",EDGE,{"derivedFrom":sQuery(id+"F2.wireOp",EDGE,"E173.MirrorC")}),-1.0]])]});
            var Q230;
            Q230=makeQuery(id+"F2.imprint","IMPRINT",FACE,{"disambiguationData":[TD([[makeQuery(id+"F2.imprint","IMPRINT",EDGE,{"derivedFrom":sQuery(id+"F2.wireOp",EDGE,"E184.MirrorC")}),-1.0]])]});
            var Q231;
            Q231=makeQuery(id+"F2.imprint","IMPRINT",FACE,{"disambiguationData":[TD([[makeQuery(id+"F2.imprint","IMPRINT",EDGE,{"derivedFrom":sQuery(id+"F2.wireOp",EDGE,"E199.MirrorC")}),1.0]])]});
            var Q232;
            Q232=makeQuery(id+"F2.imprint","IMPRINT",FACE,{"disambiguationData":[TD([[makeQuery(id+"F2.imprint","IMPRINT",EDGE,{"derivedFrom":sQuery(id+"F2.wireOp",EDGE,"E213.MirrorC")}),1.0]])]});
            var Q233;
            Q233=makeQuery(id+"F2.imprint","IMPRINT",FACE,{"disambiguationData":[TD([[makeQuery(id+"F2.imprint","IMPRINT",EDGE,{"derivedFrom":sQuery(id+"F2.wireOp",EDGE,"E118.MirrorC")}),1.0]])]});
            var Q234;
            Q234=makeQuery(id+"F2.imprint","IMPRINT",FACE,{"disambiguationData":[TD([[makeQuery(id+"F2.imprint","IMPRINT",EDGE,{"derivedFrom":sQuery(id+"F2.wireOp",EDGE,"E32.MirrorC")}),1.0]])]});
            var Q235;
            Q235=makeQuery(id+"F2.imprint","IMPRINT",FACE,{"disambiguationData":[TD([[makeQuery(id+"F2.imprint","IMPRINT",EDGE,{"derivedFrom":sQuery(id+"F2.wireOp",EDGE,"E146.MirrorC")}),1.0]])]});
            var Q236;
            Q236=makeQuery(id+"F2.imprint","IMPRINT",FACE,{"disambiguationData":[TD([[makeQuery(id+"F2.imprint","IMPRINT",EDGE,{"derivedFrom":sQuery(id+"F2.wireOp",EDGE,"E160.MirrorC")}),-1.0]])]});
            var Q237;
            Q237=makeQuery(id+"F2.imprint","IMPRINT",FACE,{"disambiguationData":[TD([[makeQuery(id+"F2.imprint","IMPRINT",EDGE,{"derivedFrom":sQuery(id+"F2.wireOp",EDGE,"E53.MirrorC")}),-1.0]])]});
            var Q238;
            Q238=makeQuery(id+"F2.imprint","IMPRINT",FACE,{"disambiguationData":[TD([[makeQuery(id+"F2.imprint","IMPRINT",EDGE,{"derivedFrom":sQuery(id+"F2.wireOp",EDGE,"E74.MirrorC")}),-1.0]])]});
            var Q239;
            Q239=makeQuery(id+"F2.imprint","IMPRINT",FACE,{"disambiguationData":[TD([[makeQuery(id+"F2.imprint","IMPRINT",EDGE,{"derivedFrom":sQuery(id+"F2.wireOp",EDGE,"E97.MirrorC")}),-1.0]])]});
            var Q240;
            Q240=makeQuery(id+"F2.imprint","IMPRINT",FACE,{"disambiguationData":[TD([[makeQuery(id+"F2.imprint","IMPRINT",EDGE,{"derivedFrom":sQuery(id+"F2.wireOp",EDGE,"E111.MirrorC")}),-1.0]])]});
            var Q241;
            Q241=makeQuery(id+"F2.imprint","IMPRINT",FACE,{"disambiguationData":[TD([[makeQuery(id+"F2.imprint","IMPRINT",EDGE,{"derivedFrom":sQuery(id+"F2.wireOp",EDGE,"E6.9.1.0")}),1.0]])]});
            var Q242;
            Q242=makeQuery(id+"F2.imprint","IMPRINT",FACE,{"disambiguationData":[TD([[makeQuery(id+"F2.imprint","IMPRINT",EDGE,{"derivedFrom":sQuery(id+"F2.wireOp",EDGE,"E6.11.5.0")}),1.0]])]});
            var Q243;
            Q243=makeQuery(id+"F2.imprint","IMPRINT",FACE,{"disambiguationData":[TD([[makeQuery(id+"F2.imprint","IMPRINT",EDGE,{"derivedFrom":sQuery(id+"F2.wireOp",EDGE,"E23.MirrorC")}),-1.0]])]});
            var Q244;
            Q244=makeQuery(id+"F2.imprint","IMPRINT",FACE,{"disambiguationData":[TD([[makeQuery(id+"F2.imprint","IMPRINT",EDGE,{"derivedFrom":sQuery(id+"F2.wireOp",EDGE,"E36.MirrorC")}),-1.0]])]});
            var Q245;
            Q245=makeQuery(id+"F2.imprint","IMPRINT",FACE,{"disambiguationData":[TD([[makeQuery(id+"F2.imprint","IMPRINT",EDGE,{"derivedFrom":sQuery(id+"F2.wireOp",EDGE,"E6.3.5.0")}),1.0]])]});
            var Q246;
            Q246=makeQuery(id+"F2.imprint","IMPRINT",FACE,{"disambiguationData":[TD([[makeQuery(id+"F2.imprint","IMPRINT",EDGE,{"derivedFrom":sQuery(id+"F2.wireOp",EDGE,"E6.6.3.0")}),1.0]])]});
            var Q247;
            Q247=makeQuery(id+"F2.imprint","IMPRINT",FACE,{"disambiguationData":[TD([[makeQuery(id+"F2.imprint","IMPRINT",EDGE,{"derivedFrom":sQuery(id+"F2.wireOp",EDGE,"E55.MirrorC")}),1.0]])]});
            var Q248;
            Q248=makeQuery(id+"F2.imprint","IMPRINT",FACE,{"disambiguationData":[TD([[makeQuery(id+"F2.imprint","IMPRINT",EDGE,{"derivedFrom":sQuery(id+"F2.wireOp",EDGE,"E182.MirrorC")}),-1.0]])]});
            var Q249;
            Q249=makeQuery(id+"F2.imprint","IMPRINT",FACE,{"disambiguationData":[TD([[makeQuery(id+"F2.imprint","IMPRINT",EDGE,{"derivedFrom":sQuery(id+"F2.wireOp",EDGE,"E197.MirrorC")}),-1.0]])]});
            var Q250;
            Q250=makeQuery(id+"F2.imprint","IMPRINT",FACE,{"disambiguationData":[TD([[makeQuery(id+"F2.imprint","IMPRINT",EDGE,{"derivedFrom":sQuery(id+"F2.wireOp",EDGE,"E211.MirrorC")}),1.0]])]});
            var Q251;
            Q251=makeQuery(id+"F2.imprint","IMPRINT",FACE,{"disambiguationData":[TD([[makeQuery(id+"F2.imprint","IMPRINT",EDGE,{"derivedFrom":sQuery(id+"F2.wireOp",EDGE,"E116.MirrorC")}),-1.0]])]});
            var Q252;
            Q252=makeQuery(id+"F2.imprint","IMPRINT",FACE,{"disambiguationData":[TD([[makeQuery(id+"F2.imprint","IMPRINT",EDGE,{"derivedFrom":sQuery(id+"F2.wireOp",EDGE,"E130.MirrorC")}),-1.0]])]});
            var Q253;
            Q253=makeQuery(id+"F2.imprint","IMPRINT",FACE,{"disambiguationData":[TD([[makeQuery(id+"F2.imprint","IMPRINT",EDGE,{"derivedFrom":sQuery(id+"F2.wireOp",EDGE,"E144.MirrorC")}),-1.0]])]});
            var Q254;
            Q254=makeQuery(id+"F2.imprint","IMPRINT",FACE,{"disambiguationData":[TD([[makeQuery(id+"F2.imprint","IMPRINT",EDGE,{"derivedFrom":sQuery(id+"F2.wireOp",EDGE,"E158.MirrorC")}),1.0]])]});
            var Q255;
            Q255=makeQuery(id+"F2.imprint","IMPRINT",FACE,{"disambiguationData":[TD([[makeQuery(id+"F2.imprint","IMPRINT",EDGE,{"derivedFrom":sQuery(id+"F2.wireOp",EDGE,"E51.MirrorC")}),-1.0]])]});
            var Q256;
            Q256=makeQuery(id+"F2.imprint","IMPRINT",FACE,{"disambiguationData":[TD([[makeQuery(id+"F2.imprint","IMPRINT",EDGE,{"derivedFrom":sQuery(id+"F2.wireOp",EDGE,"E72.MirrorC")}),-1.0]])]});
            var Q257;
            Q257=makeQuery(id+"F2.imprint","IMPRINT",FACE,{"disambiguationData":[TD([[makeQuery(id+"F2.imprint","IMPRINT",EDGE,{"derivedFrom":sQuery(id+"F2.wireOp",EDGE,"E95.MirrorC")}),1.0]])]});
            var Q258;
            Q258=makeQuery(id+"F2.imprint","IMPRINT",FACE,{"disambiguationData":[TD([[makeQuery(id+"F2.imprint","IMPRINT",EDGE,{"derivedFrom":sQuery(id+"F2.wireOp",EDGE,"E109.MirrorC")}),-1.0]])]});
            var Q259;
            Q259=makeQuery(id+"F2.imprint","IMPRINT",FACE,{"disambiguationData":[TD([[makeQuery(id+"F2.imprint","IMPRINT",EDGE,{"derivedFrom":sQuery(id+"F2.wireOp",EDGE,"E6.8.5.0")}),1.0]])]});
            var Q260;
            Q260=makeQuery(id+"F2.imprint","IMPRINT",FACE,{"disambiguationData":[TD([[makeQuery(id+"F2.imprint","IMPRINT",EDGE,{"derivedFrom":sQuery(id+"F2.wireOp",EDGE,"E6.11.3.0")}),1.0]])]});
            var Q261;
            Q261=makeQuery(id+"F2.imprint","IMPRINT",FACE,{"disambiguationData":[TD([[makeQuery(id+"F2.imprint","IMPRINT",EDGE,{"derivedFrom":sQuery(id+"F2.wireOp",EDGE,"E21.MirrorC")}),-1.0]])]});
            var Q262;
            Q262=makeQuery(id+"F2.imprint","IMPRINT",FACE,{"disambiguationData":[TD([[makeQuery(id+"F2.imprint","IMPRINT",EDGE,{"derivedFrom":sQuery(id+"F2.wireOp",EDGE,"E33.MirrorC")}),-1.0]])]});
            var Q263;
            Q263=makeQuery(id+"F2.imprint","IMPRINT",FACE,{"disambiguationData":[TD([[makeQuery(id+"F2.imprint","IMPRINT",EDGE,{"derivedFrom":sQuery(id+"F2.wireOp",EDGE,"E6.6.1.0")}),1.0]])]});
            var Q264;
            Q264=makeQuery(id+"F2.imprint","IMPRINT",FACE,{"disambiguationData":[TD([[makeQuery(id+"F2.imprint","IMPRINT",EDGE,{"derivedFrom":sQuery(id+"F2.wireOp",EDGE,"E171.MirrorC")}),1.0]])]});
            var Q265;
            Q265=makeQuery(id+"F2.imprint","IMPRINT",FACE,{"disambiguationData":[TD([[makeQuery(id+"F2.imprint","IMPRINT",EDGE,{"derivedFrom":sQuery(id+"F2.wireOp",EDGE,"E181.MirrorC")}),1.0]])]});
            var Q266;
            Q266=makeQuery(id+"F2.imprint","IMPRINT",FACE,{"disambiguationData":[TD([[makeQuery(id+"F2.imprint","IMPRINT",EDGE,{"derivedFrom":sQuery(id+"F2.wireOp",EDGE,"E196.MirrorC")}),1.0]])]});
            var Q267;
            Q267=makeQuery(id+"F2.imprint","IMPRINT",FACE,{"disambiguationData":[TD([[makeQuery(id+"F2.imprint","IMPRINT",EDGE,{"derivedFrom":sQuery(id+"F2.wireOp",EDGE,"E210.MirrorC")}),1.0]])]});
            var Q268;
            Q268=makeQuery(id+"F2.imprint","IMPRINT",FACE,{"disambiguationData":[TD([[makeQuery(id+"F2.imprint","IMPRINT",EDGE,{"derivedFrom":sQuery(id+"F2.wireOp",EDGE,"E6.2.0.0")}),-1.0]])]});
            var Q269;
            Q269=makeQuery(id+"F2.imprint","IMPRINT",FACE,{"disambiguationData":[TD([[makeQuery(id+"F2.imprint","IMPRINT",EDGE,{"derivedFrom":sQuery(id+"F2.wireOp",EDGE,"E129.MirrorC")}),-1.0]])]});
            var Q270;
            Q270=makeQuery(id+"F2.imprint","IMPRINT",FACE,{"disambiguationData":[TD([[makeQuery(id+"F2.imprint","IMPRINT",EDGE,{"derivedFrom":sQuery(id+"F2.wireOp",EDGE,"E143.MirrorC")}),1.0]])]});
            var Q271;
            Q271=makeQuery(id+"F2.imprint","IMPRINT",FACE,{"disambiguationData":[TD([[makeQuery(id+"F2.imprint","IMPRINT",EDGE,{"derivedFrom":sQuery(id+"F2.wireOp",EDGE,"E157.MirrorC")}),-1.0]])]});
            var Q272;
            Q272=makeQuery(id+"F2.imprint","IMPRINT",FACE,{"disambiguationData":[TD([[makeQuery(id+"F2.imprint","IMPRINT",EDGE,{"derivedFrom":sQuery(id+"F2.wireOp",EDGE,"E50.MirrorC")}),-1.0]])]});
            var Q273;
            Q273=makeQuery(id+"F2.imprint","IMPRINT",FACE,{"disambiguationData":[TD([[makeQuery(id+"F2.imprint","IMPRINT",EDGE,{"derivedFrom":sQuery(id+"F2.wireOp",EDGE,"E71.MirrorC")}),-1.0]])]});
            var Q274;
            Q274=makeQuery(id+"F2.imprint","IMPRINT",FACE,{"disambiguationData":[TD([[makeQuery(id+"F2.imprint","IMPRINT",EDGE,{"derivedFrom":sQuery(id+"F2.wireOp",EDGE,"E94.MirrorC")}),1.0]])]});
            var Q275;
            Q275=makeQuery(id+"F2.imprint","IMPRINT",FACE,{"disambiguationData":[TD([[makeQuery(id+"F2.imprint","IMPRINT",EDGE,{"derivedFrom":sQuery(id+"F2.wireOp",EDGE,"E108.MirrorC")}),-1.0]])]});
            var Q276;
            Q276=makeQuery(id+"F2.imprint","IMPRINT",FACE,{"disambiguationData":[TD([[makeQuery(id+"F2.imprint","IMPRINT",EDGE,{"derivedFrom":sQuery(id+"F2.wireOp",EDGE,"E6.8.4.0")}),1.0]])]});
            var Q277;
            Q277=makeQuery(id+"F2.imprint","IMPRINT",FACE,{"disambiguationData":[TD([[makeQuery(id+"F2.imprint","IMPRINT",EDGE,{"derivedFrom":sQuery(id+"F2.wireOp",EDGE,"E6.11.2.0")}),1.0]])]});
            var Q278;
            Q278=makeQuery(id+"F2.imprint","IMPRINT",FACE,{"disambiguationData":[TD([[makeQuery(id+"F2.imprint","IMPRINT",EDGE,{"derivedFrom":sQuery(id+"F2.wireOp",EDGE,"E20.MirrorC")}),-1.0]])]});
            var Q279;
            Q279=makeQuery(id+"F2.imprint","IMPRINT",FACE,{"disambiguationData":[TD([[makeQuery(id+"F2.imprint","IMPRINT",EDGE,{"derivedFrom":sQuery(id+"F2.wireOp",EDGE,"E31.MirrorC")}),-1.0]])]});
            var Q280;
            Q280=makeQuery(id+"F2.imprint","IMPRINT",FACE,{"disambiguationData":[TD([[makeQuery(id+"F2.imprint","IMPRINT",EDGE,{"derivedFrom":sQuery(id+"F2.wireOp",EDGE,"E6.5.6.0")}),1.0]])]});
            var Q281;
            Q281=makeQuery(id+"F2.imprint","IMPRINT",FACE,{"disambiguationData":[TD([[makeQuery(id+"F2.imprint","IMPRINT",EDGE,{"derivedFrom":sQuery(id+"F2.wireOp",EDGE,"E73.MirrorC")}),-1.0]])]});
            var Q282;
            Q282=makeQuery(id+"F2.imprint","IMPRINT",FACE,{"disambiguationData":[TD([[makeQuery(id+"F2.imprint","IMPRINT",EDGE,{"derivedFrom":sQuery(id+"F2.wireOp",EDGE,"E96.MirrorC")}),1.0]])]});
            var Q283;
            Q283=makeQuery(id+"F2.imprint","IMPRINT",FACE,{"disambiguationData":[TD([[makeQuery(id+"F2.imprint","IMPRINT",EDGE,{"derivedFrom":sQuery(id+"F2.wireOp",EDGE,"E110.MirrorC")}),-1.0]])]});
            var Q284;
            Q284=makeQuery(id+"F2.imprint","IMPRINT",FACE,{"disambiguationData":[TD([[makeQuery(id+"F2.imprint","IMPRINT",EDGE,{"derivedFrom":sQuery(id+"F2.wireOp",EDGE,"E117.MirrorC")}),1.0]])]});
            var Q285;
            Q285=makeQuery(id+"F2.imprint","IMPRINT",FACE,{"disambiguationData":[TD([[makeQuery(id+"F2.imprint","IMPRINT",EDGE,{"derivedFrom":sQuery(id+"F2.wireOp",EDGE,"E6.11.4.0")}),1.0]])]});
            var Q286;
            Q286=makeQuery(id+"F2.imprint","IMPRINT",FACE,{"disambiguationData":[TD([[makeQuery(id+"F2.imprint","IMPRINT",EDGE,{"derivedFrom":sQuery(id+"F2.wireOp",EDGE,"E22.MirrorC")}),-1.0]])]});
            var Q287;
            Q287=makeQuery(id+"F2.imprint","IMPRINT",FACE,{"disambiguationData":[TD([[makeQuery(id+"F2.imprint","IMPRINT",EDGE,{"derivedFrom":sQuery(id+"F2.wireOp",EDGE,"E35.MirrorC")}),-1.0]])]});
            var Q288;
            Q288=makeQuery(id+"F2.imprint","IMPRINT",FACE,{"disambiguationData":[TD([[makeQuery(id+"F2.imprint","IMPRINT",EDGE,{"derivedFrom":sQuery(id+"F2.wireOp",EDGE,"E52.MirrorC")}),-1.0]])]});
            var Q289;
            Q289=makeQuery(id+"F2.imprint","IMPRINT",FACE,{"disambiguationData":[TD([[makeQuery(id+"F2.imprint","IMPRINT",EDGE,{"derivedFrom":sQuery(id+"F2.wireOp",EDGE,"E6.6.2.0")}),1.0]])]});
            var Q290;
            Q290=makeQuery(id+"F2.imprint","IMPRINT",FACE,{"disambiguationData":[TD([[makeQuery(id+"F2.imprint","IMPRINT",EDGE,{"derivedFrom":sQuery(id+"F2.wireOp",EDGE,"E6.8.6.0")}),1.0]])]});
            var Q291;
            Q291=makeQuery(id+"F2.imprint","IMPRINT",FACE,{"disambiguationData":[TD([[makeQuery(id+"F2.imprint","IMPRINT",EDGE,{"derivedFrom":sQuery(id+"F2.wireOp",EDGE,"E183.MirrorC")}),-1.0]])]});
            var Q292;
            Q292=makeQuery(id+"F2.imprint","IMPRINT",FACE,{"disambiguationData":[TD([[makeQuery(id+"F2.imprint","IMPRINT",EDGE,{"derivedFrom":sQuery(id+"F2.wireOp",EDGE,"E198.MirrorC")}),1.0]])]});
            var Q293;
            Q293=makeQuery(id+"F2.imprint","IMPRINT",FACE,{"disambiguationData":[TD([[makeQuery(id+"F2.imprint","IMPRINT",EDGE,{"derivedFrom":sQuery(id+"F2.wireOp",EDGE,"E212.MirrorC")}),1.0]])]});
            var Q294;
            Q294=makeQuery(id+"F2.imprint","IMPRINT",FACE,{"disambiguationData":[TD([[makeQuery(id+"F2.imprint","IMPRINT",EDGE,{"derivedFrom":sQuery(id+"F2.wireOp",EDGE,"E131.MirrorC")}),-1.0]])]});
            var Q295;
            Q295=makeQuery(id+"F2.imprint","IMPRINT",FACE,{"disambiguationData":[TD([[makeQuery(id+"F2.imprint","IMPRINT",EDGE,{"derivedFrom":sQuery(id+"F2.wireOp",EDGE,"E145.MirrorC")}),-1.0]])]});
            var Q296;
            Q296=makeQuery(id+"F2.imprint","IMPRINT",FACE,{"disambiguationData":[TD([[makeQuery(id+"F2.imprint","IMPRINT",EDGE,{"derivedFrom":sQuery(id+"F2.wireOp",EDGE,"E159.MirrorC")}),1.0]])]});
            var Q297;
            Q297=makeQuery(id+"F2.imprint","IMPRINT",FACE,{"disambiguationData":[TD([[makeQuery(id+"F2.imprint","IMPRINT",EDGE,{"derivedFrom":sQuery(id+"F2.wireOp",EDGE,"E172.MirrorC")}),-1.0]])]});
            var Q298;
            Q298=makeQuery(id+"F2.imprint","IMPRINT",FACE,{"disambiguationData":[TD([[makeQuery(id+"F2.imprint","IMPRINT",EDGE,{"derivedFrom":sQuery(id+"F2.wireOp",EDGE,"E5")}),-1.0]])]});
            extrude(context, id + "F3", {"entities" : qUnion([Q0, Q1, Q2, Q3, Q4, Q5, Q6, Q7, Q8, Q9, Q10, Q11, Q12, Q13, Q14, Q15, Q16, Q17, Q18, Q19, Q20, Q21, Q22, Q23, Q24, Q25, Q26, Q27, Q28, Q29, Q30, Q31, Q32, Q33, Q34, Q35, Q36, Q37, Q38, Q39, Q40, Q41, Q42, Q43, Q44, Q45, Q46, Q47, Q48, Q49, Q50, Q51, Q52, Q53, Q54, Q55, Q56, Q57, Q58, Q59, Q60, Q61, Q62, Q63, Q64, Q65, Q66, Q67, Q68, Q69, Q70, Q71, Q72, Q73, Q74, Q75, Q76, Q77, Q78, Q79, Q80, Q81, Q82, Q83, Q84, Q85, Q86, Q87, Q88, Q89, Q90, Q91, Q92, Q93, Q94, Q95, Q96, Q97, Q98, Q99, Q100, Q101, Q102, Q103, Q104, Q105, Q106, Q107, Q108, Q109, Q110, Q111, Q112, Q113, Q114, Q115, Q116, Q117, Q118, Q119, Q120, Q121, Q122, Q123, Q124, Q125, Q126, Q127, Q128, Q129, Q130, Q131, Q132, Q133, Q134, Q135, Q136, Q137, Q138, Q139, Q140, Q141, Q142, Q143, Q144, Q145, Q146, Q147, Q148, Q149, Q150, Q151, Q152, Q153, Q154, Q155, Q156, Q157, Q158, Q159, Q160, Q161, Q162, Q163, Q164, Q165, Q166, Q167, Q168, Q169, Q170, Q171, Q172, Q173, Q174, Q175, Q176, Q177, Q178, Q179, Q180, Q181, Q182, Q183, Q184, Q185, Q186, Q187, Q188, Q189, Q190, Q191, Q192, Q193, Q194, Q195, Q196, Q197, Q198, Q199, Q200, Q201, Q202, Q203, Q204, Q205, Q206, Q207, Q208, Q209, Q210, Q211, Q212, Q213, Q214, Q215, Q216, Q217, Q218, Q219, Q220, Q221, Q222, Q223, Q224, Q225, Q226, Q227, Q228, Q229, Q230, Q231, Q232, Q233, Q234, Q235, Q236, Q237, Q238, Q239, Q240, Q241, Q242, Q243, Q244, Q245, Q246, Q247, Q248, Q249, Q250, Q251, Q252, Q253, Q254, Q255, Q256, Q257, Q258, Q259, Q260, Q261, Q262, Q263, Q264, Q265, Q266, Q267, Q268, Q269, Q270, Q271, Q272, Q273, Q274, Q275, Q276, Q277, Q278, Q279, Q280, Q281, Q282, Q283, Q284, Q285, Q286, Q287, Q288, Q289, Q290, Q291, Q292, Q293, Q294, Q295, Q296, Q297, Q298]), "operationType" : NewBodyOperationType.REMOVE, "oppositeDirection" : true, "depth" : 25 * mm});
        }
    });
